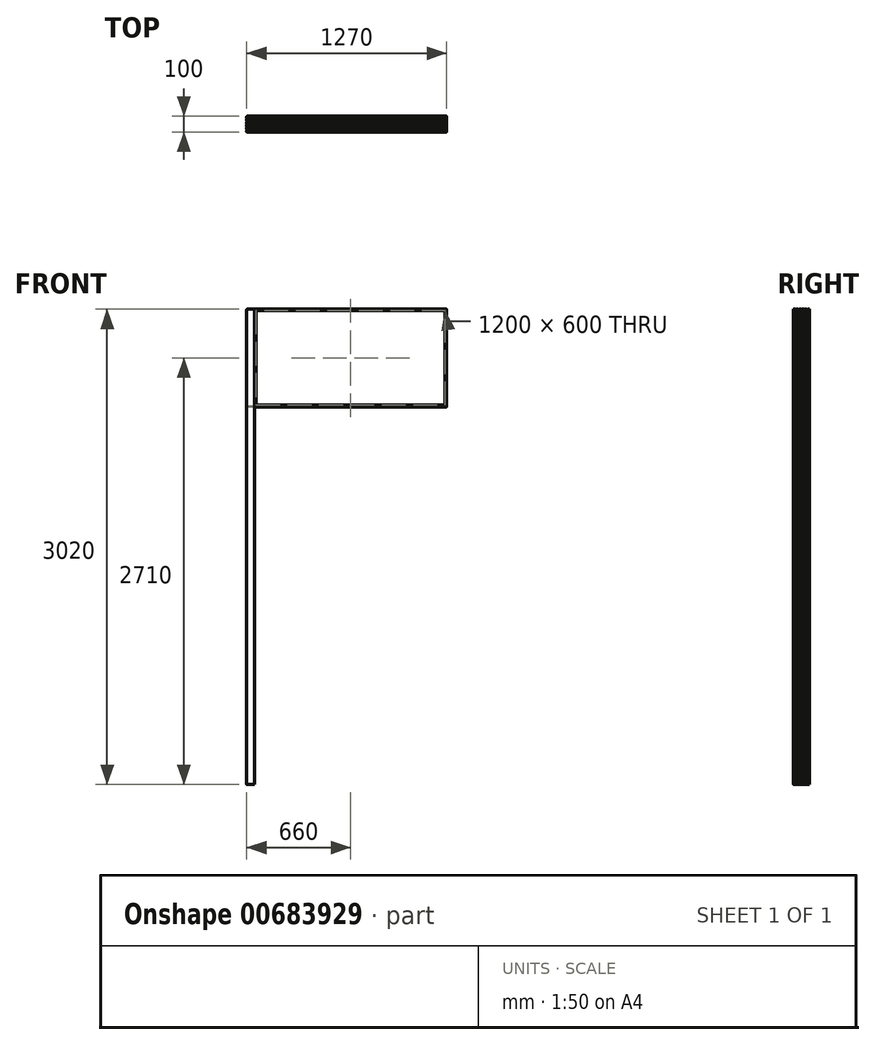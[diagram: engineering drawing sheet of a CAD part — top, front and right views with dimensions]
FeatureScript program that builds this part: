
annotation { "Feature Type Name" : "Feature", "Feature Type Description" : "" }
export const myFeature = defineFeature(function(context is Context, id is Id, definition is map)
    precondition{}
    {
        {
            var Q0;
            Q0=qCreatedBy(makeId("Front.planeOp"),FACE);
            var sketch = newSketch(context, id + "F0", { "sketchPlane" : qUnion([Q0])});
            skLineSegment(sketch, "E0.bottom", {"start": v(-2550, 0) * mm, "end": v(-2500, 0) * mm});
            skLineSegment(sketch, "E0.top", {"start": v(-2550, -3020) * mm, "end": v(-2500, -3020) * mm});
            skLineSegment(sketch, "E0.left", {"start": v(-2550, 0) * mm, "end": v(-2550, -3020) * mm});
            skLineSegment(sketch, "E0.right", {"start": v(-2500, 0) * mm, "end": v(-2500, -3020) * mm});
            skLineSegment(sketch, "E1.MirrorCS", {"start": v(2550, -3020) * mm, "end": v(2500, -3020) * mm});
            skLineSegment(sketch, "E2.MirrorCS", {"start": v(2500, 0) * mm, "end": v(2500, -3020) * mm});
            skLineSegment(sketch, "E3.MirrorCS", {"start": v(2550, 0) * mm, "end": v(2500, 0) * mm});
            skLineSegment(sketch, "E4.MirrorCS", {"start": v(2550, 0) * mm, "end": v(2550, -3020) * mm});
            skSolve(sketch);
        }
        {
            var Q0;
            Q0 = qSketchRegion(id + "F0", true);
            extrude(context, id + "F1", {"entities" : qUnion([Q0]), "depth" : 100 * mm, "offsetDistance" : 25 * mm});
        }
        {
            var Q0;
            Q0=makeQuery(id+"F1.opExtrude","SWEPT_FACE",FACE,{"disambiguationData":[OSD([sQuery(id+"F0.wireOp",EDGE,"E0.bottom")])]});
            var sketch = newSketch(context, id + "F2", { "sketchPlane" : qUnion([Q0])});
            skLineSegment(sketch, "E5.bottom", {"start": v(-2550, -100) * mm, "end": v(-3770, -100) * mm});
            skLineSegment(sketch, "E5.top", {"start": v(-2550, 0) * mm, "end": v(-3770, 0) * mm});
            skLineSegment(sketch, "E5.left", {"start": v(-2550, -100) * mm, "end": v(-2550, 0) * mm});
            skLineSegment(sketch, "E5.right", {"start": v(-3770, -100) * mm, "end": v(-3770, 0) * mm});
            skLineSegment(sketch, "E6.bottom", {"start": v(-2500, -100) * mm, "end": v(2500, -100) * mm});
            skLineSegment(sketch, "E6.top", {"start": v(-2500, 0) * mm, "end": v(2500, 0) * mm});
            skLineSegment(sketch, "E6.left", {"start": v(-2500, -100) * mm, "end": v(-2500, 0) * mm});
            skLineSegment(sketch, "E6.right", {"start": v(2500, -100) * mm, "end": v(2500, 0) * mm});
            skLineSegment(sketch, "E7.bottom", {"start": v(2550, -100) * mm, "end": v(3770, -100) * mm});
            skLineSegment(sketch, "E7.top", {"start": v(2550, 0) * mm, "end": v(3770, 0) * mm});
            skLineSegment(sketch, "E7.left", {"start": v(2550, -100) * mm, "end": v(2550, 0) * mm});
            skLineSegment(sketch, "E7.right", {"start": v(3770, -100) * mm, "end": v(3770, 0) * mm});
            skSolve(sketch);
        }
        {
            var Q0;
            Q0 = qSketchRegion(id + "F2", true);
            extrude(context, id + "F3", {"entities" : qUnion([Q0]), "oppositeDirection" : true, "depth" : 620 * mm, "offsetDistance" : 25 * mm});
        }
        {
            var Q0;
            Q0=makeQuery(id+"F3.opExtrude","SWEPT_FACE",FACE,{"disambiguationData":[OSD([sQuery(id+"F2.wireOp",EDGE,"E6.bottom")])]});
            var sketch = newSketch(context, id + "F4", { "sketchPlane" : qUnion([Q0])});
            skLineSegment(sketch, "E8.0", {"start": v(-2560, -10) * mm, "end": v(-3760, -10) * mm});
            skLineSegment(sketch, "E8.1", {"start": v(-2560, -610) * mm, "end": v(-2560, -10) * mm});
            skLineSegment(sketch, "E8.2", {"start": v(-3760, -610) * mm, "end": v(-2560, -610) * mm});
            skLineSegment(sketch, "E8.3", {"start": v(-3760, -10) * mm, "end": v(-3760, -610) * mm});
            skLineSegment(sketch, "E9.0", {"start": v(2490, -10) * mm, "end": v(-2490, -10) * mm});
            skLineSegment(sketch, "E9.1", {"start": v(2490, -610) * mm, "end": v(2490, -10) * mm});
            skLineSegment(sketch, "E9.2", {"start": v(-2490, -610) * mm, "end": v(2490, -610) * mm});
            skLineSegment(sketch, "E9.3", {"start": v(-2490, -10) * mm, "end": v(-2490, -610) * mm});
            skLineSegment(sketch, "E10.0", {"start": v(3760, -10) * mm, "end": v(2560, -10) * mm});
            skLineSegment(sketch, "E10.1", {"start": v(3760, -610) * mm, "end": v(3760, -10) * mm});
            skLineSegment(sketch, "E10.2", {"start": v(2560, -610) * mm, "end": v(3760, -610) * mm});
            skLineSegment(sketch, "E10.3", {"start": v(2560, -10) * mm, "end": v(2560, -610) * mm});
            skSolve(sketch);
        }
        {
            var Q0;
            Q0 = qSketchRegion(id + "F4", true);
            extrude(context, id + "F5", {"entities" : qUnion([Q0]), "operationType" : NewBodyOperationType.REMOVE, "endBound" : BoundingType.THROUGH_ALL, "oppositeDirection" : true, "depth" : 25 * mm, "offsetDistance" : 25 * mm});
        }
        {
            var Q0;
            Q0=makeQuery(id+"F3.opExtrude","SWEPT_FACE",FACE,{"disambiguationData":[OSD([sQuery(id+"F2.wireOp",EDGE,"E5.right")])]});
            var sketch = newSketch(context, id + "F6", { "sketchPlane" : qUnion([Q0])});
            skLineSegment(sketch, "E11", {"start": v(10, 0) * mm, "end": v(10, -2) * mm});
            skLineSegment(sketch, "E12", {"start": v(10, -2) * mm, "end": v(18, -2) * mm});
            skLineSegment(sketch, "E13", {"start": v(18, -2) * mm, "end": v(18, 0) * mm});
            skLineSegment(sketch, "E14.1.0.0", {"start": v(36, -2) * mm, "end": v(36, 0) * mm});
            skLineSegment(sketch, "E14.1.0.1", {"start": v(28, -2) * mm, "end": v(36, -2) * mm});
            skLineSegment(sketch, "E14.1.0.2", {"start": v(28, 0) * mm, "end": v(28, -2) * mm});
            skLineSegment(sketch, "E14.2.0.0", {"start": v(54, -2) * mm, "end": v(54, 0) * mm});
            skLineSegment(sketch, "E14.2.0.1", {"start": v(46, -2) * mm, "end": v(54, -2) * mm});
            skLineSegment(sketch, "E14.2.0.2", {"start": v(46, 0) * mm, "end": v(46, -2) * mm});
            skLineSegment(sketch, "E14.3.0.0", {"start": v(72, -2) * mm, "end": v(72, 0) * mm});
            skLineSegment(sketch, "E14.3.0.1", {"start": v(64, -2) * mm, "end": v(72, -2) * mm});
            skLineSegment(sketch, "E14.3.0.2", {"start": v(64, 0) * mm, "end": v(64, -2) * mm});
            skLineSegment(sketch, "E14.4.0.0", {"start": v(90, -2) * mm, "end": v(90, 0) * mm});
            skLineSegment(sketch, "E14.4.0.1", {"start": v(82, -2) * mm, "end": v(90, -2) * mm});
            skLineSegment(sketch, "E14.4.0.2", {"start": v(82, 0) * mm, "end": v(82, -2) * mm});
            skLineSegment(sketch, "E14.direction1", {"start": v(10, -2) * mm, "end": v(28, -2) * mm, "construction": true});
            skLineSegment(sketch, "E15", {"start": v(10, 0) * mm, "end": v(18, 0) * mm});
            skLineSegment(sketch, "E16", {"start": v(28, 0) * mm, "end": v(36, 0) * mm});
            skLineSegment(sketch, "E17", {"start": v(46, 0) * mm, "end": v(54, 0) * mm});
            skLineSegment(sketch, "E18", {"start": v(64, 0) * mm, "end": v(72, 0) * mm});
            skLineSegment(sketch, "E19", {"start": v(82, 0) * mm, "end": v(90, 0) * mm});
            skLineSegment(sketch, "E20", {"start": v(100, -310) * mm, "end": v(0, -310) * mm, "construction": true});
            skLineSegment(sketch, "E21.MirrorCS", {"start": v(90, -618) * mm, "end": v(90, -620) * mm});
            skLineSegment(sketch, "E22.MirrorCS", {"start": v(64, -620) * mm, "end": v(64, -618) * mm});
            skLineSegment(sketch, "E23.MirrorCS", {"start": v(10, -620) * mm, "end": v(10, -618) * mm});
            skLineSegment(sketch, "E24.MirrorCS", {"start": v(18, -618) * mm, "end": v(18, -620) * mm});
            skLineSegment(sketch, "E25.MirrorCS", {"start": v(36, -618) * mm, "end": v(36, -620) * mm});
            skLineSegment(sketch, "E26.MirrorCS", {"start": v(28, -620) * mm, "end": v(28, -618) * mm});
            skLineSegment(sketch, "E27.MirrorCS", {"start": v(54, -618) * mm, "end": v(54, -620) * mm});
            skLineSegment(sketch, "E28.MirrorCS", {"start": v(46, -620) * mm, "end": v(46, -618) * mm});
            skLineSegment(sketch, "E29.MirrorCS", {"start": v(72, -618) * mm, "end": v(72, -620) * mm});
            skLineSegment(sketch, "E30.MirrorCS", {"start": v(82, -620) * mm, "end": v(82, -618) * mm});
            skLineSegment(sketch, "E31.MirrorCS", {"start": v(10, -620) * mm, "end": v(18, -620) * mm});
            skLineSegment(sketch, "E32.MirrorCS", {"start": v(10, -618) * mm, "end": v(18, -618) * mm});
            skLineSegment(sketch, "E33.MirrorCS", {"start": v(64, -618) * mm, "end": v(72, -618) * mm});
            skLineSegment(sketch, "E34.MirrorCS", {"start": v(64, -620) * mm, "end": v(72, -620) * mm});
            skLineSegment(sketch, "E35.MirrorCS", {"start": v(82, -620) * mm, "end": v(90, -620) * mm});
            skLineSegment(sketch, "E36.MirrorCS", {"start": v(28, -620) * mm, "end": v(36, -620) * mm});
            skLineSegment(sketch, "E37.MirrorCS", {"start": v(82, -618) * mm, "end": v(90, -618) * mm});
            skLineSegment(sketch, "E38.MirrorCS", {"start": v(10, -618) * mm, "end": v(28, -618) * mm, "construction": true});
            skLineSegment(sketch, "E39.MirrorCS", {"start": v(46, -620) * mm, "end": v(54, -620) * mm});
            skLineSegment(sketch, "E40.MirrorCS", {"start": v(28, -618) * mm, "end": v(36, -618) * mm});
            skLineSegment(sketch, "E41.MirrorCS", {"start": v(46, -618) * mm, "end": v(54, -618) * mm});
            skSolve(sketch);
        }
        {
            var Q0;
            Q0 = qSketchRegion(id + "F6", true);
            extrude(context, id + "F7", {"entities" : qUnion([Q0]), "operationType" : NewBodyOperationType.REMOVE, "endBound" : BoundingType.THROUGH_ALL, "oppositeDirection" : true, "depth" : 25 * mm, "offsetDistance" : 25 * mm});
        }
        {
            var Q0;
            {var subQ0=sQuery(id+"F2.wireOp",EDGE,"E5.top");var subQ1=sQuery(id+"F2.wireOp",EDGE,"E5.left");var subQ2=sQuery(id+"F2.wireOp",EDGE,"E5.right");Q0=makeQuery(id+"F7.boolean.opBoolean","SPLIT",FACE,{"disambiguationData":[TD([makeQuery(id+"F3.opExtrude","SWEPT_FACE",FACE,{"disambiguationData":[OSD([subQ0])]})])],"derivedFrom":makeQuery(id+"F3.opExtrude","CAP_FACE",FACE,{"disambiguationData":[OSD([sQuery(id+"F2.wireOp",EDGE,"E5.bottom"),subQ0,subQ1,subQ2])],"isStart":true})});}
            var sketch = newSketch(context, id + "F8", { "sketchPlane" : qUnion([Q0])});
            skLineSegment(sketch, "E42.bottom", {"start": v(-3768, -90) * mm, "end": v(-3770, -90) * mm});
            skLineSegment(sketch, "E42.top", {"start": v(-3768, -82) * mm, "end": v(-3770, -82) * mm});
            skLineSegment(sketch, "E42.left", {"start": v(-3768, -90) * mm, "end": v(-3768, -82) * mm});
            skLineSegment(sketch, "E42.right", {"start": v(-3770, -90) * mm, "end": v(-3770, -82) * mm});
            skLineSegment(sketch, "E43.0.1.0", {"start": v(-3768, -64) * mm, "end": v(-3770, -64) * mm});
            skLineSegment(sketch, "E43.0.1.1", {"start": v(-3768, -72) * mm, "end": v(-3770, -72) * mm});
            skLineSegment(sketch, "E43.0.1.2", {"start": v(-3770, -72) * mm, "end": v(-3770, -64) * mm});
            skLineSegment(sketch, "E43.0.1.3", {"start": v(-3768, -72) * mm, "end": v(-3768, -64) * mm});
            skLineSegment(sketch, "E43.0.2.0", {"start": v(-3768, -46) * mm, "end": v(-3770, -46) * mm});
            skLineSegment(sketch, "E43.0.2.1", {"start": v(-3768, -54) * mm, "end": v(-3770, -54) * mm});
            skLineSegment(sketch, "E43.0.2.2", {"start": v(-3770, -54) * mm, "end": v(-3770, -46) * mm});
            skLineSegment(sketch, "E43.0.2.3", {"start": v(-3768, -54) * mm, "end": v(-3768, -46) * mm});
            skLineSegment(sketch, "E43.0.3.0", {"start": v(-3768, -28) * mm, "end": v(-3770, -28) * mm});
            skLineSegment(sketch, "E43.0.3.1", {"start": v(-3768, -36) * mm, "end": v(-3770, -36) * mm});
            skLineSegment(sketch, "E43.0.3.2", {"start": v(-3770, -36) * mm, "end": v(-3770, -28) * mm});
            skLineSegment(sketch, "E43.0.3.3", {"start": v(-3768, -36) * mm, "end": v(-3768, -28) * mm});
            skLineSegment(sketch, "E43.0.4.0", {"start": v(-3768, -10) * mm, "end": v(-3770, -10) * mm});
            skLineSegment(sketch, "E43.0.4.1", {"start": v(-3768, -18) * mm, "end": v(-3770, -18) * mm});
            skLineSegment(sketch, "E43.0.4.2", {"start": v(-3770, -18) * mm, "end": v(-3770, -10) * mm});
            skLineSegment(sketch, "E43.0.4.3", {"start": v(-3768, -18) * mm, "end": v(-3768, -10) * mm});
            skLineSegment(sketch, "E43.direction1", {"start": v(-3770, -90) * mm, "end": v(-2770, -90) * mm, "construction": true});
            skLineSegment(sketch, "E43.direction2", {"start": v(-3770, -90) * mm, "end": v(-3770, -72) * mm, "construction": true});
            skPoint(sketch, "E44.0", {"position": v(0, -10) * mm});
            skLineSegment(sketch, "E45.MirrorCS", {"start": v(3768, -64) * mm, "end": v(3770, -64) * mm});
            skLineSegment(sketch, "E46.MirrorCS", {"start": v(3768, -36) * mm, "end": v(3770, -36) * mm});
            skLineSegment(sketch, "E47.MirrorCS", {"start": v(3768, -90) * mm, "end": v(3770, -90) * mm});
            skLineSegment(sketch, "E48.MirrorCS", {"start": v(3768, -82) * mm, "end": v(3770, -82) * mm});
            skLineSegment(sketch, "E49.MirrorCS", {"start": v(3768, -72) * mm, "end": v(3770, -72) * mm});
            skLineSegment(sketch, "E50.MirrorCS", {"start": v(3768, -46) * mm, "end": v(3770, -46) * mm});
            skLineSegment(sketch, "E51.MirrorCS", {"start": v(3768, -54) * mm, "end": v(3770, -54) * mm});
            skLineSegment(sketch, "E52.MirrorCS", {"start": v(3770, -36) * mm, "end": v(3770, -28) * mm});
            skLineSegment(sketch, "E53.MirrorCS", {"start": v(3768, -90) * mm, "end": v(3768, -82) * mm});
            skLineSegment(sketch, "E54.MirrorCS", {"start": v(3770, -72) * mm, "end": v(3770, -64) * mm});
            skLineSegment(sketch, "E55.MirrorCS", {"start": v(3770, -54) * mm, "end": v(3770, -46) * mm});
            skLineSegment(sketch, "E56.MirrorCS", {"start": v(3768, -36) * mm, "end": v(3768, -28) * mm});
            skLineSegment(sketch, "E57.MirrorCS", {"start": v(3770, -90) * mm, "end": v(3770, -82) * mm});
            skLineSegment(sketch, "E58.MirrorCS", {"start": v(3768, -72) * mm, "end": v(3768, -64) * mm});
            skLineSegment(sketch, "E59.MirrorCS", {"start": v(3768, -54) * mm, "end": v(3768, -46) * mm});
            skLineSegment(sketch, "E60.MirrorCS", {"start": v(3768, -28) * mm, "end": v(3770, -28) * mm});
            skLineSegment(sketch, "E61.MirrorCS", {"start": v(3770, -90) * mm, "end": v(3770, -72) * mm, "construction": true});
            skLineSegment(sketch, "E62.MirrorCS", {"start": v(3770, -90) * mm, "end": v(2770, -90) * mm, "construction": true});
            skLineSegment(sketch, "E63.MirrorCS", {"start": v(3768, -18) * mm, "end": v(3770, -18) * mm});
            skLineSegment(sketch, "E64.MirrorCS", {"start": v(3770, -18) * mm, "end": v(3770, -10) * mm});
            skLineSegment(sketch, "E65.MirrorCS", {"start": v(3768, -18) * mm, "end": v(3768, -10) * mm});
            skLineSegment(sketch, "E66.MirrorCS", {"start": v(3768, -10) * mm, "end": v(3770, -10) * mm});
            skSolve(sketch);
        }
        {
            var Q0;
            Q0 = qSketchRegion(id + "F8", true);
            extrude(context, id + "F9", {"entities" : qUnion([Q0]), "operationType" : NewBodyOperationType.REMOVE, "endBound" : BoundingType.THROUGH_ALL, "oppositeDirection" : true, "depth" : 25 * mm, "offsetDistance" : 25 * mm});
        }
        {
            var Q0;
            Q0=makeQuery(id+"F3.opExtrude","SWEPT_FACE",FACE,{"disambiguationData":[OSD([sQuery(id+"F2.wireOp",EDGE,"E7.top")])]});
            cPlane(context, id + "F10", {"entities" : qUnion([Q0]), "cplaneType" : CPlaneType.OFFSET, "offset" : 1 * mm, "oppositeDirection" : true, "width" : 150 * mm, "height" : 150 * mm});
        }
        {
            var Q0;
            Q0=qCreatedBy(id+"F10.planeOp",FACE);
            var sketch = newSketch(context, id + "F11", { "sketchPlane" : qUnion([Q0])});
            skLineSegment(sketch, "E67.0", {"start": v(2490, -10) * mm, "end": v(2490, -610) * mm});
            skLineSegment(sketch, "E67.1", {"start": v(-2490, -10) * mm, "end": v(2490, -10) * mm});
            skLineSegment(sketch, "E67.2", {"start": v(2490, -610) * mm, "end": v(-2490, -610) * mm});
            skLineSegment(sketch, "E67.3", {"start": v(-2490, -610) * mm, "end": v(-2490, -10) * mm});
            skLineSegment(sketch, "E67.4", {"start": v(-2560, -10) * mm, "end": v(-2560, -610) * mm});
            skLineSegment(sketch, "E67.5", {"start": v(-2560, -610) * mm, "end": v(-3760, -610) * mm});
            skLineSegment(sketch, "E67.6", {"start": v(-3760, -10) * mm, "end": v(-2560, -10) * mm});
            skLineSegment(sketch, "E67.7", {"start": v(-3760, -610) * mm, "end": v(-3760, -10) * mm});
            skLineSegment(sketch, "E67.8", {"start": v(2560, -10) * mm, "end": v(2560, -610) * mm});
            skLineSegment(sketch, "E67.9", {"start": v(2560, -610) * mm, "end": v(3760, -610) * mm});
            skLineSegment(sketch, "E67.10", {"start": v(3760, -10) * mm, "end": v(2560, -10) * mm});
            skLineSegment(sketch, "E67.11", {"start": v(3760, -610) * mm, "end": v(3760, -10) * mm});
            skSolve(sketch);
        }
        {
            var Q0;
            Q0 = qSketchRegion(id + "F11", true);
            var Q1;
            Q1=makeQuery(id+"F3.opExtrude","SWEPT_FACE",FACE,{"disambiguationData":[OSD([sQuery(id+"F2.wireOp",EDGE,"E5.bottom")])]});
            extrude(context, id + "F12", {"entities" : qUnion([Q0]), "endBound" : BoundingType.UP_TO_SURFACE, "oppositeDirection" : true, "depth" : 25 * mm, "endBoundEntityFace" : qUnion([Q1]), "hasOffset" : true, "offsetDistance" : 1 * mm});
        }
        {
            var Q0;
            {var subQ0=sQuery(id+"F2.wireOp",EDGE,"E7.right");var subQ1=sQuery(id+"F2.wireOp",EDGE,"E7.top");Q0=makeQuery(id+"F7.boolean.opBoolean","SPLIT",EDGE,{"disambiguationData":[TD([makeQuery(id+"F3.opExtrude","SWEPT_FACE",FACE,{"disambiguationData":[OSD([subQ1])]})])],"derivedFrom":makeQuery(id+"F3.opExtrude","CAP_EDGE",EDGE,{"disambiguationData":[OSD([subQ0])],"isStart":true})});}
            var Q1;
            {var subQ0=sQuery(id+"F2.wireOp",EDGE,"E7.right");Q1=makeQuery(id+"F7.boolean.opBoolean","SPLIT",EDGE,{"disambiguationData":[TD([makeQuery(id+"F7.opExtrude","SWEPT_FACE",FACE,{"disambiguationData":[OSD([sQuery(id+"F6.wireOp",EDGE,"E13")])]})])],"derivedFrom":makeQuery(id+"F3.opExtrude","CAP_EDGE",EDGE,{"disambiguationData":[OSD([subQ0])],"isStart":true})});}
            var Q2;
            {var subQ0=sQuery(id+"F2.wireOp",EDGE,"E7.right");Q2=makeQuery(id+"F7.boolean.opBoolean","SPLIT",EDGE,{"disambiguationData":[TD([makeQuery(id+"F7.opExtrude","SWEPT_FACE",FACE,{"disambiguationData":[OSD([sQuery(id+"F6.wireOp",EDGE,"E14.1.0.0")])]})])],"derivedFrom":makeQuery(id+"F3.opExtrude","CAP_EDGE",EDGE,{"disambiguationData":[OSD([subQ0])],"isStart":true})});}
            var Q3;
            {var subQ0=sQuery(id+"F2.wireOp",EDGE,"E7.right");Q3=makeQuery(id+"F7.boolean.opBoolean","SPLIT",EDGE,{"disambiguationData":[TD([makeQuery(id+"F7.opExtrude","SWEPT_FACE",FACE,{"disambiguationData":[OSD([sQuery(id+"F6.wireOp",EDGE,"E14.2.0.0")])]})])],"derivedFrom":makeQuery(id+"F3.opExtrude","CAP_EDGE",EDGE,{"disambiguationData":[OSD([subQ0])],"isStart":true})});}
            var Q4;
            {var subQ0=sQuery(id+"F2.wireOp",EDGE,"E7.right");Q4=makeQuery(id+"F7.boolean.opBoolean","SPLIT",EDGE,{"disambiguationData":[TD([makeQuery(id+"F7.opExtrude","SWEPT_FACE",FACE,{"disambiguationData":[OSD([sQuery(id+"F6.wireOp",EDGE,"E14.3.0.0")])]})])],"derivedFrom":makeQuery(id+"F3.opExtrude","CAP_EDGE",EDGE,{"disambiguationData":[OSD([subQ0])],"isStart":true})});}
            var Q5;
            {var subQ0=sQuery(id+"F2.wireOp",EDGE,"E7.bottom");var subQ1=sQuery(id+"F2.wireOp",EDGE,"E7.right");Q5=makeQuery(id+"F7.boolean.opBoolean","SPLIT",EDGE,{"disambiguationData":[TD([makeQuery(id+"F3.opExtrude","SWEPT_FACE",FACE,{"disambiguationData":[OSD([subQ0])]})])],"derivedFrom":makeQuery(id+"F3.opExtrude","CAP_EDGE",EDGE,{"disambiguationData":[OSD([subQ1])],"isStart":true})});}
            var Q6;
            Q6=makeQuery(id+"F9.boolean.opBoolean","INTERSECT",EDGE,{"derivedFrom":[makeQuery(id+"F7.boolean.opBoolean","COPY",FACE,{"disambiguationData":[TD([makeQuery(id+"F3.opExtrude","SWEPT_FACE",FACE,{"disambiguationData":[OSD([sQuery(id+"F2.wireOp",EDGE,"E7.left")])]})])],"derivedFrom":makeQuery(id+"F7.opExtrude","SWEPT_FACE",FACE,{"disambiguationData":[OSD([sQuery(id+"F6.wireOp",EDGE,"E14.4.0.1")])]})}),makeQuery(id+"F9.opExtrude","SWEPT_FACE",FACE,{"disambiguationData":[OSD([sQuery(id+"F8.wireOp",EDGE,"E53.MirrorCS")])]})]});
            var Q7;
            Q7=makeQuery(id+"F9.boolean.opBoolean","INTERSECT",EDGE,{"derivedFrom":[makeQuery(id+"F7.boolean.opBoolean","COPY",FACE,{"disambiguationData":[TD([makeQuery(id+"F3.opExtrude","SWEPT_FACE",FACE,{"disambiguationData":[OSD([sQuery(id+"F2.wireOp",EDGE,"E7.left")])]})])],"derivedFrom":makeQuery(id+"F7.opExtrude","SWEPT_FACE",FACE,{"disambiguationData":[OSD([sQuery(id+"F6.wireOp",EDGE,"E14.3.0.1")])]})}),makeQuery(id+"F9.opExtrude","SWEPT_FACE",FACE,{"disambiguationData":[OSD([sQuery(id+"F8.wireOp",EDGE,"E58.MirrorCS")])]})]});
            var Q8;
            Q8=makeQuery(id+"F9.boolean.opBoolean","INTERSECT",EDGE,{"derivedFrom":[makeQuery(id+"F7.boolean.opBoolean","COPY",FACE,{"disambiguationData":[TD([makeQuery(id+"F3.opExtrude","SWEPT_FACE",FACE,{"disambiguationData":[OSD([sQuery(id+"F2.wireOp",EDGE,"E7.left")])]})])],"derivedFrom":makeQuery(id+"F7.opExtrude","SWEPT_FACE",FACE,{"disambiguationData":[OSD([sQuery(id+"F6.wireOp",EDGE,"E14.2.0.1")])]})}),makeQuery(id+"F9.opExtrude","SWEPT_FACE",FACE,{"disambiguationData":[OSD([sQuery(id+"F8.wireOp",EDGE,"E59.MirrorCS")])]})]});
            var Q9;
            Q9=makeQuery(id+"F9.boolean.opBoolean","INTERSECT",EDGE,{"derivedFrom":[makeQuery(id+"F7.boolean.opBoolean","COPY",FACE,{"disambiguationData":[TD([makeQuery(id+"F3.opExtrude","SWEPT_FACE",FACE,{"disambiguationData":[OSD([sQuery(id+"F2.wireOp",EDGE,"E7.left")])]})])],"derivedFrom":makeQuery(id+"F7.opExtrude","SWEPT_FACE",FACE,{"disambiguationData":[OSD([sQuery(id+"F6.wireOp",EDGE,"E14.1.0.1")])]})}),makeQuery(id+"F9.opExtrude","SWEPT_FACE",FACE,{"disambiguationData":[OSD([sQuery(id+"F8.wireOp",EDGE,"E56.MirrorCS")])]})]});
            var Q10;
            Q10=makeQuery(id+"F9.boolean.opBoolean","INTERSECT",EDGE,{"derivedFrom":[makeQuery(id+"F7.boolean.opBoolean","COPY",FACE,{"disambiguationData":[TD([makeQuery(id+"F3.opExtrude","SWEPT_FACE",FACE,{"disambiguationData":[OSD([sQuery(id+"F2.wireOp",EDGE,"E7.left")])]})])],"derivedFrom":makeQuery(id+"F7.opExtrude","SWEPT_FACE",FACE,{"disambiguationData":[OSD([sQuery(id+"F6.wireOp",EDGE,"E12")])]})}),makeQuery(id+"F9.opExtrude","SWEPT_FACE",FACE,{"disambiguationData":[OSD([sQuery(id+"F8.wireOp",EDGE,"E65.MirrorCS")])]})]});
            var Q11;
            {var subQ0=sQuery(id+"F2.wireOp",EDGE,"E7.left");var subQ1=sQuery(id+"F2.wireOp",EDGE,"E7.top");Q11=makeQuery(id+"F7.boolean.opBoolean","SPLIT",EDGE,{"disambiguationData":[TD([makeQuery(id+"F3.opExtrude","SWEPT_FACE",FACE,{"disambiguationData":[OSD([subQ1])]})])],"derivedFrom":makeQuery(id+"F3.opExtrude","CAP_EDGE",EDGE,{"disambiguationData":[OSD([subQ0])],"isStart":true})});}
            var Q12;
            {var subQ0=sQuery(id+"F2.wireOp",EDGE,"E7.left");Q12=makeQuery(id+"F7.boolean.opBoolean","SPLIT",EDGE,{"disambiguationData":[TD([makeQuery(id+"F7.opExtrude","SWEPT_FACE",FACE,{"disambiguationData":[OSD([sQuery(id+"F6.wireOp",EDGE,"E13")])]})])],"derivedFrom":makeQuery(id+"F3.opExtrude","CAP_EDGE",EDGE,{"disambiguationData":[OSD([subQ0])],"isStart":true})});}
            var Q13;
            {var subQ0=sQuery(id+"F2.wireOp",EDGE,"E7.left");Q13=makeQuery(id+"F7.boolean.opBoolean","SPLIT",EDGE,{"disambiguationData":[TD([makeQuery(id+"F7.opExtrude","SWEPT_FACE",FACE,{"disambiguationData":[OSD([sQuery(id+"F6.wireOp",EDGE,"E14.1.0.0")])]})])],"derivedFrom":makeQuery(id+"F3.opExtrude","CAP_EDGE",EDGE,{"disambiguationData":[OSD([subQ0])],"isStart":true})});}
            var Q14;
            {var subQ0=sQuery(id+"F2.wireOp",EDGE,"E7.left");Q14=makeQuery(id+"F7.boolean.opBoolean","SPLIT",EDGE,{"disambiguationData":[TD([makeQuery(id+"F7.opExtrude","SWEPT_FACE",FACE,{"disambiguationData":[OSD([sQuery(id+"F6.wireOp",EDGE,"E14.2.0.0")])]})])],"derivedFrom":makeQuery(id+"F3.opExtrude","CAP_EDGE",EDGE,{"disambiguationData":[OSD([subQ0])],"isStart":true})});}
            var Q15;
            {var subQ0=sQuery(id+"F2.wireOp",EDGE,"E7.bottom");var subQ1=sQuery(id+"F2.wireOp",EDGE,"E7.left");Q15=makeQuery(id+"F7.boolean.opBoolean","SPLIT",EDGE,{"disambiguationData":[TD([makeQuery(id+"F3.opExtrude","SWEPT_FACE",FACE,{"disambiguationData":[OSD([subQ0])]})])],"derivedFrom":makeQuery(id+"F3.opExtrude","CAP_EDGE",EDGE,{"disambiguationData":[OSD([subQ1])],"isStart":true})});}
            var Q16;
            Q16=makeQuery(id+"F1.opExtrude","SWEPT_EDGE",EDGE,{"disambiguationData":[OSD([sQuery(id+"F0.wireOp",EDGE,"E3.MirrorCS"),sQuery(id+"F0.wireOp",EDGE,"E4.MirrorCS")])]});
            var Q17;
            {var subQ0=sQuery(id+"F2.wireOp",EDGE,"E7.left");Q17=makeQuery(id+"F7.boolean.opBoolean","SPLIT",EDGE,{"disambiguationData":[TD([makeQuery(id+"F7.opExtrude","SWEPT_FACE",FACE,{"disambiguationData":[OSD([sQuery(id+"F6.wireOp",EDGE,"E14.3.0.0")])]})])],"derivedFrom":makeQuery(id+"F3.opExtrude","CAP_EDGE",EDGE,{"disambiguationData":[OSD([subQ0])],"isStart":true})});}
            var Q18;
            Q18=makeQuery(id+"F7.boolean.opBoolean","INTERSECT",EDGE,{"derivedFrom":[makeQuery(id+"F3.opExtrude","SWEPT_FACE",FACE,{"disambiguationData":[OSD([sQuery(id+"F2.wireOp",EDGE,"E7.left")])]}),makeQuery(id+"F7.opExtrude","SWEPT_FACE",FACE,{"disambiguationData":[OSD([sQuery(id+"F6.wireOp",EDGE,"E14.4.0.1")])]})]});
            var Q19;
            Q19=makeQuery(id+"F7.boolean.opBoolean","INTERSECT",EDGE,{"derivedFrom":[makeQuery(id+"F3.opExtrude","SWEPT_FACE",FACE,{"disambiguationData":[OSD([sQuery(id+"F2.wireOp",EDGE,"E7.left")])]}),makeQuery(id+"F7.opExtrude","SWEPT_FACE",FACE,{"disambiguationData":[OSD([sQuery(id+"F6.wireOp",EDGE,"E14.3.0.1")])]})]});
            var Q20;
            Q20=makeQuery(id+"F7.boolean.opBoolean","INTERSECT",EDGE,{"derivedFrom":[makeQuery(id+"F3.opExtrude","SWEPT_FACE",FACE,{"disambiguationData":[OSD([sQuery(id+"F2.wireOp",EDGE,"E7.left")])]}),makeQuery(id+"F7.opExtrude","SWEPT_FACE",FACE,{"disambiguationData":[OSD([sQuery(id+"F6.wireOp",EDGE,"E14.2.0.1")])]})]});
            var Q21;
            Q21=makeQuery(id+"F7.boolean.opBoolean","INTERSECT",EDGE,{"derivedFrom":[makeQuery(id+"F3.opExtrude","SWEPT_FACE",FACE,{"disambiguationData":[OSD([sQuery(id+"F2.wireOp",EDGE,"E7.left")])]}),makeQuery(id+"F7.opExtrude","SWEPT_FACE",FACE,{"disambiguationData":[OSD([sQuery(id+"F6.wireOp",EDGE,"E14.1.0.1")])]})]});
            var Q22;
            Q22=makeQuery(id+"F7.boolean.opBoolean","INTERSECT",EDGE,{"derivedFrom":[makeQuery(id+"F3.opExtrude","SWEPT_FACE",FACE,{"disambiguationData":[OSD([sQuery(id+"F2.wireOp",EDGE,"E7.left")])]}),makeQuery(id+"F7.opExtrude","SWEPT_FACE",FACE,{"disambiguationData":[OSD([sQuery(id+"F6.wireOp",EDGE,"E12")])]})]});
            var Q23;
            Q23=makeQuery(id+"F1.opExtrude","SWEPT_FACE",FACE,{"disambiguationData":[OSD([sQuery(id+"F0.wireOp",EDGE,"E3.MirrorCS")])]});
            var Q24;
            {var subQ0=sQuery(id+"F2.wireOp",EDGE,"E6.right");Q24=makeQuery(id+"F7.boolean.opBoolean","SPLIT",EDGE,{"disambiguationData":[TD([makeQuery(id+"F7.opExtrude","SWEPT_FACE",FACE,{"disambiguationData":[OSD([sQuery(id+"F6.wireOp",EDGE,"E14.1.0.0")])]})])],"derivedFrom":makeQuery(id+"F3.opExtrude","CAP_EDGE",EDGE,{"disambiguationData":[OSD([subQ0])],"isStart":true})});}
            var Q25;
            {var subQ0=sQuery(id+"F2.wireOp",EDGE,"E6.right");Q25=makeQuery(id+"F7.boolean.opBoolean","SPLIT",EDGE,{"disambiguationData":[TD([makeQuery(id+"F7.opExtrude","SWEPT_FACE",FACE,{"disambiguationData":[OSD([sQuery(id+"F6.wireOp",EDGE,"E13")])]})])],"derivedFrom":makeQuery(id+"F3.opExtrude","CAP_EDGE",EDGE,{"disambiguationData":[OSD([subQ0])],"isStart":true})});}
            var Q26;
            {var subQ0=sQuery(id+"F2.wireOp",EDGE,"E6.right");var subQ1=sQuery(id+"F2.wireOp",EDGE,"E6.top");Q26=makeQuery(id+"F7.boolean.opBoolean","SPLIT",EDGE,{"disambiguationData":[TD([makeQuery(id+"F3.opExtrude","SWEPT_FACE",FACE,{"disambiguationData":[OSD([subQ1])]})])],"derivedFrom":makeQuery(id+"F3.opExtrude","CAP_EDGE",EDGE,{"disambiguationData":[OSD([subQ0])],"isStart":true})});}
            var Q27;
            {var subQ0=sQuery(id+"F2.wireOp",EDGE,"E6.right");Q27=makeQuery(id+"F7.boolean.opBoolean","SPLIT",EDGE,{"disambiguationData":[TD([makeQuery(id+"F7.opExtrude","SWEPT_FACE",FACE,{"disambiguationData":[OSD([sQuery(id+"F6.wireOp",EDGE,"E14.2.0.0")])]})])],"derivedFrom":makeQuery(id+"F3.opExtrude","CAP_EDGE",EDGE,{"disambiguationData":[OSD([subQ0])],"isStart":true})});}
            var Q28;
            {var subQ0=sQuery(id+"F2.wireOp",EDGE,"E6.right");Q28=makeQuery(id+"F7.boolean.opBoolean","SPLIT",EDGE,{"disambiguationData":[TD([makeQuery(id+"F7.opExtrude","SWEPT_FACE",FACE,{"disambiguationData":[OSD([sQuery(id+"F6.wireOp",EDGE,"E14.3.0.0")])]})])],"derivedFrom":makeQuery(id+"F3.opExtrude","CAP_EDGE",EDGE,{"disambiguationData":[OSD([subQ0])],"isStart":true})});}
            var Q29;
            {var subQ0=sQuery(id+"F2.wireOp",EDGE,"E6.bottom");var subQ1=sQuery(id+"F2.wireOp",EDGE,"E6.right");Q29=makeQuery(id+"F7.boolean.opBoolean","SPLIT",EDGE,{"disambiguationData":[TD([makeQuery(id+"F3.opExtrude","SWEPT_FACE",FACE,{"disambiguationData":[OSD([subQ0])]})])],"derivedFrom":makeQuery(id+"F3.opExtrude","CAP_EDGE",EDGE,{"disambiguationData":[OSD([subQ1])],"isStart":true})});}
            var Q30;
            Q30=makeQuery(id+"F7.boolean.opBoolean","INTERSECT",EDGE,{"derivedFrom":[makeQuery(id+"F3.opExtrude","SWEPT_FACE",FACE,{"disambiguationData":[OSD([sQuery(id+"F2.wireOp",EDGE,"E6.right")])]}),makeQuery(id+"F7.opExtrude","SWEPT_FACE",FACE,{"disambiguationData":[OSD([sQuery(id+"F6.wireOp",EDGE,"E14.4.0.1")])]})]});
            var Q31;
            Q31=makeQuery(id+"F7.boolean.opBoolean","INTERSECT",EDGE,{"derivedFrom":[makeQuery(id+"F3.opExtrude","SWEPT_FACE",FACE,{"disambiguationData":[OSD([sQuery(id+"F2.wireOp",EDGE,"E6.right")])]}),makeQuery(id+"F7.opExtrude","SWEPT_FACE",FACE,{"disambiguationData":[OSD([sQuery(id+"F6.wireOp",EDGE,"E14.3.0.1")])]})]});
            var Q32;
            Q32=makeQuery(id+"F7.boolean.opBoolean","INTERSECT",EDGE,{"derivedFrom":[makeQuery(id+"F3.opExtrude","SWEPT_FACE",FACE,{"disambiguationData":[OSD([sQuery(id+"F2.wireOp",EDGE,"E6.right")])]}),makeQuery(id+"F7.opExtrude","SWEPT_FACE",FACE,{"disambiguationData":[OSD([sQuery(id+"F6.wireOp",EDGE,"E14.2.0.1")])]})]});
            var Q33;
            Q33=makeQuery(id+"F7.boolean.opBoolean","INTERSECT",EDGE,{"derivedFrom":[makeQuery(id+"F3.opExtrude","SWEPT_FACE",FACE,{"disambiguationData":[OSD([sQuery(id+"F2.wireOp",EDGE,"E6.right")])]}),makeQuery(id+"F7.opExtrude","SWEPT_FACE",FACE,{"disambiguationData":[OSD([sQuery(id+"F6.wireOp",EDGE,"E14.1.0.1")])]})]});
            var Q34;
            Q34=makeQuery(id+"F7.boolean.opBoolean","INTERSECT",EDGE,{"derivedFrom":[makeQuery(id+"F3.opExtrude","SWEPT_FACE",FACE,{"disambiguationData":[OSD([sQuery(id+"F2.wireOp",EDGE,"E6.right")])]}),makeQuery(id+"F7.opExtrude","SWEPT_FACE",FACE,{"disambiguationData":[OSD([sQuery(id+"F6.wireOp",EDGE,"E12")])]})]});
            var Q35;
            {var subQ0=sQuery(id+"F2.wireOp",EDGE,"E7.right");var subQ1=sQuery(id+"F2.wireOp",EDGE,"E7.top");Q35=makeQuery(id+"F7.boolean.opBoolean","SPLIT",EDGE,{"disambiguationData":[TD([makeQuery(id+"F3.opExtrude","SWEPT_FACE",FACE,{"disambiguationData":[OSD([subQ1])]})])],"derivedFrom":makeQuery(id+"F3.opExtrude","CAP_EDGE",EDGE,{"disambiguationData":[OSD([subQ0])],"isStart":false})});}
            var Q36;
            Q36=makeQuery(id+"F9.boolean.opBoolean","INTERSECT",EDGE,{"derivedFrom":[makeQuery(id+"F7.boolean.opBoolean","COPY",FACE,{"disambiguationData":[TD([makeQuery(id+"F3.opExtrude","SWEPT_FACE",FACE,{"disambiguationData":[OSD([sQuery(id+"F2.wireOp",EDGE,"E7.left")])]})])],"derivedFrom":makeQuery(id+"F7.opExtrude","SWEPT_FACE",FACE,{"disambiguationData":[OSD([sQuery(id+"F6.wireOp",EDGE,"E32.MirrorCS")])]})}),makeQuery(id+"F9.opExtrude","SWEPT_FACE",FACE,{"disambiguationData":[OSD([sQuery(id+"F8.wireOp",EDGE,"E65.MirrorCS")])]})]});
            var Q37;
            {var subQ0=sQuery(id+"F2.wireOp",EDGE,"E7.right");Q37=makeQuery(id+"F7.boolean.opBoolean","SPLIT",EDGE,{"disambiguationData":[TD([makeQuery(id+"F7.opExtrude","SWEPT_FACE",FACE,{"disambiguationData":[OSD([sQuery(id+"F6.wireOp",EDGE,"E24.MirrorCS")])]})])],"derivedFrom":makeQuery(id+"F3.opExtrude","CAP_EDGE",EDGE,{"disambiguationData":[OSD([subQ0])],"isStart":false})});}
            var Q38;
            Q38=makeQuery(id+"F9.boolean.opBoolean","INTERSECT",EDGE,{"derivedFrom":[makeQuery(id+"F7.boolean.opBoolean","COPY",FACE,{"disambiguationData":[TD([makeQuery(id+"F3.opExtrude","SWEPT_FACE",FACE,{"disambiguationData":[OSD([sQuery(id+"F2.wireOp",EDGE,"E7.left")])]})])],"derivedFrom":makeQuery(id+"F7.opExtrude","SWEPT_FACE",FACE,{"disambiguationData":[OSD([sQuery(id+"F6.wireOp",EDGE,"E40.MirrorCS")])]})}),makeQuery(id+"F9.opExtrude","SWEPT_FACE",FACE,{"disambiguationData":[OSD([sQuery(id+"F8.wireOp",EDGE,"E56.MirrorCS")])]})]});
            var Q39;
            {var subQ0=sQuery(id+"F2.wireOp",EDGE,"E7.right");Q39=makeQuery(id+"F7.boolean.opBoolean","SPLIT",EDGE,{"disambiguationData":[TD([makeQuery(id+"F7.opExtrude","SWEPT_FACE",FACE,{"disambiguationData":[OSD([sQuery(id+"F6.wireOp",EDGE,"E25.MirrorCS")])]})])],"derivedFrom":makeQuery(id+"F3.opExtrude","CAP_EDGE",EDGE,{"disambiguationData":[OSD([subQ0])],"isStart":false})});}
            var Q40;
            Q40=makeQuery(id+"F9.boolean.opBoolean","INTERSECT",EDGE,{"derivedFrom":[makeQuery(id+"F7.boolean.opBoolean","COPY",FACE,{"disambiguationData":[TD([makeQuery(id+"F3.opExtrude","SWEPT_FACE",FACE,{"disambiguationData":[OSD([sQuery(id+"F2.wireOp",EDGE,"E7.left")])]})])],"derivedFrom":makeQuery(id+"F7.opExtrude","SWEPT_FACE",FACE,{"disambiguationData":[OSD([sQuery(id+"F6.wireOp",EDGE,"E41.MirrorCS")])]})}),makeQuery(id+"F9.opExtrude","SWEPT_FACE",FACE,{"disambiguationData":[OSD([sQuery(id+"F8.wireOp",EDGE,"E59.MirrorCS")])]})]});
            var Q41;
            {var subQ0=sQuery(id+"F2.wireOp",EDGE,"E7.right");Q41=makeQuery(id+"F7.boolean.opBoolean","SPLIT",EDGE,{"disambiguationData":[TD([makeQuery(id+"F7.opExtrude","SWEPT_FACE",FACE,{"disambiguationData":[OSD([sQuery(id+"F6.wireOp",EDGE,"E22.MirrorCS")])]})])],"derivedFrom":makeQuery(id+"F3.opExtrude","CAP_EDGE",EDGE,{"disambiguationData":[OSD([subQ0])],"isStart":false})});}
            var Q42;
            Q42=makeQuery(id+"F9.boolean.opBoolean","INTERSECT",EDGE,{"derivedFrom":[makeQuery(id+"F7.boolean.opBoolean","COPY",FACE,{"disambiguationData":[TD([makeQuery(id+"F3.opExtrude","SWEPT_FACE",FACE,{"disambiguationData":[OSD([sQuery(id+"F2.wireOp",EDGE,"E7.left")])]})])],"derivedFrom":makeQuery(id+"F7.opExtrude","SWEPT_FACE",FACE,{"disambiguationData":[OSD([sQuery(id+"F6.wireOp",EDGE,"E33.MirrorCS")])]})}),makeQuery(id+"F9.opExtrude","SWEPT_FACE",FACE,{"disambiguationData":[OSD([sQuery(id+"F8.wireOp",EDGE,"E58.MirrorCS")])]})]});
            var Q43;
            {var subQ0=sQuery(id+"F2.wireOp",EDGE,"E7.right");Q43=makeQuery(id+"F7.boolean.opBoolean","SPLIT",EDGE,{"disambiguationData":[TD([makeQuery(id+"F7.opExtrude","SWEPT_FACE",FACE,{"disambiguationData":[OSD([sQuery(id+"F6.wireOp",EDGE,"E29.MirrorCS")])]})])],"derivedFrom":makeQuery(id+"F3.opExtrude","CAP_EDGE",EDGE,{"disambiguationData":[OSD([subQ0])],"isStart":false})});}
            var Q44;
            Q44=makeQuery(id+"F9.boolean.opBoolean","INTERSECT",EDGE,{"derivedFrom":[makeQuery(id+"F7.boolean.opBoolean","COPY",FACE,{"disambiguationData":[TD([makeQuery(id+"F3.opExtrude","SWEPT_FACE",FACE,{"disambiguationData":[OSD([sQuery(id+"F2.wireOp",EDGE,"E7.left")])]})])],"derivedFrom":makeQuery(id+"F7.opExtrude","SWEPT_FACE",FACE,{"disambiguationData":[OSD([sQuery(id+"F6.wireOp",EDGE,"E37.MirrorCS")])]})}),makeQuery(id+"F9.opExtrude","SWEPT_FACE",FACE,{"disambiguationData":[OSD([sQuery(id+"F8.wireOp",EDGE,"E53.MirrorCS")])]})]});
            var Q45;
            {var subQ0=sQuery(id+"F2.wireOp",EDGE,"E7.bottom");var subQ1=sQuery(id+"F2.wireOp",EDGE,"E7.right");Q45=makeQuery(id+"F7.boolean.opBoolean","SPLIT",EDGE,{"disambiguationData":[TD([makeQuery(id+"F3.opExtrude","SWEPT_FACE",FACE,{"disambiguationData":[OSD([subQ0])]})])],"derivedFrom":makeQuery(id+"F3.opExtrude","CAP_EDGE",EDGE,{"disambiguationData":[OSD([subQ1])],"isStart":false})});}
            var Q46;
            {var subQ0=sQuery(id+"F2.wireOp",EDGE,"E7.left");var subQ1=sQuery(id+"F2.wireOp",EDGE,"E7.top");Q46=makeQuery(id+"F7.boolean.opBoolean","SPLIT",EDGE,{"disambiguationData":[TD([makeQuery(id+"F3.opExtrude","SWEPT_FACE",FACE,{"disambiguationData":[OSD([subQ1])]})])],"derivedFrom":makeQuery(id+"F3.opExtrude","CAP_EDGE",EDGE,{"disambiguationData":[OSD([subQ0])],"isStart":false})});}
            var Q47;
            Q47=makeQuery(id+"F7.boolean.opBoolean","INTERSECT",EDGE,{"derivedFrom":[makeQuery(id+"F3.opExtrude","SWEPT_FACE",FACE,{"disambiguationData":[OSD([sQuery(id+"F2.wireOp",EDGE,"E7.left")])]}),makeQuery(id+"F7.opExtrude","SWEPT_FACE",FACE,{"disambiguationData":[OSD([sQuery(id+"F6.wireOp",EDGE,"E32.MirrorCS")])]})]});
            var Q48;
            {var subQ0=sQuery(id+"F2.wireOp",EDGE,"E7.left");Q48=makeQuery(id+"F7.boolean.opBoolean","SPLIT",EDGE,{"disambiguationData":[TD([makeQuery(id+"F7.opExtrude","SWEPT_FACE",FACE,{"disambiguationData":[OSD([sQuery(id+"F6.wireOp",EDGE,"E24.MirrorCS")])]})])],"derivedFrom":makeQuery(id+"F3.opExtrude","CAP_EDGE",EDGE,{"disambiguationData":[OSD([subQ0])],"isStart":false})});}
            var Q49;
            Q49=makeQuery(id+"F7.boolean.opBoolean","INTERSECT",EDGE,{"derivedFrom":[makeQuery(id+"F3.opExtrude","SWEPT_FACE",FACE,{"disambiguationData":[OSD([sQuery(id+"F2.wireOp",EDGE,"E7.left")])]}),makeQuery(id+"F7.opExtrude","SWEPT_FACE",FACE,{"disambiguationData":[OSD([sQuery(id+"F6.wireOp",EDGE,"E40.MirrorCS")])]})]});
            var Q50;
            {var subQ0=sQuery(id+"F2.wireOp",EDGE,"E7.left");Q50=makeQuery(id+"F7.boolean.opBoolean","SPLIT",EDGE,{"disambiguationData":[TD([makeQuery(id+"F7.opExtrude","SWEPT_FACE",FACE,{"disambiguationData":[OSD([sQuery(id+"F6.wireOp",EDGE,"E25.MirrorCS")])]})])],"derivedFrom":makeQuery(id+"F3.opExtrude","CAP_EDGE",EDGE,{"disambiguationData":[OSD([subQ0])],"isStart":false})});}
            var Q51;
            Q51=makeQuery(id+"F7.boolean.opBoolean","INTERSECT",EDGE,{"derivedFrom":[makeQuery(id+"F3.opExtrude","SWEPT_FACE",FACE,{"disambiguationData":[OSD([sQuery(id+"F2.wireOp",EDGE,"E7.left")])]}),makeQuery(id+"F7.opExtrude","SWEPT_FACE",FACE,{"disambiguationData":[OSD([sQuery(id+"F6.wireOp",EDGE,"E41.MirrorCS")])]})]});
            var Q52;
            {var subQ0=sQuery(id+"F2.wireOp",EDGE,"E7.left");Q52=makeQuery(id+"F7.boolean.opBoolean","SPLIT",EDGE,{"disambiguationData":[TD([makeQuery(id+"F7.opExtrude","SWEPT_FACE",FACE,{"disambiguationData":[OSD([sQuery(id+"F6.wireOp",EDGE,"E22.MirrorCS")])]})])],"derivedFrom":makeQuery(id+"F3.opExtrude","CAP_EDGE",EDGE,{"disambiguationData":[OSD([subQ0])],"isStart":false})});}
            var Q53;
            Q53=makeQuery(id+"F7.boolean.opBoolean","INTERSECT",EDGE,{"derivedFrom":[makeQuery(id+"F3.opExtrude","SWEPT_FACE",FACE,{"disambiguationData":[OSD([sQuery(id+"F2.wireOp",EDGE,"E7.left")])]}),makeQuery(id+"F7.opExtrude","SWEPT_FACE",FACE,{"disambiguationData":[OSD([sQuery(id+"F6.wireOp",EDGE,"E33.MirrorCS")])]})]});
            var Q54;
            {var subQ0=sQuery(id+"F2.wireOp",EDGE,"E7.left");Q54=makeQuery(id+"F7.boolean.opBoolean","SPLIT",EDGE,{"disambiguationData":[TD([makeQuery(id+"F7.opExtrude","SWEPT_FACE",FACE,{"disambiguationData":[OSD([sQuery(id+"F6.wireOp",EDGE,"E29.MirrorCS")])]})])],"derivedFrom":makeQuery(id+"F3.opExtrude","CAP_EDGE",EDGE,{"disambiguationData":[OSD([subQ0])],"isStart":false})});}
            var Q55;
            Q55=makeQuery(id+"F7.boolean.opBoolean","INTERSECT",EDGE,{"derivedFrom":[makeQuery(id+"F3.opExtrude","SWEPT_FACE",FACE,{"disambiguationData":[OSD([sQuery(id+"F2.wireOp",EDGE,"E7.left")])]}),makeQuery(id+"F7.opExtrude","SWEPT_FACE",FACE,{"disambiguationData":[OSD([sQuery(id+"F6.wireOp",EDGE,"E37.MirrorCS")])]})]});
            var Q56;
            {var subQ0=sQuery(id+"F2.wireOp",EDGE,"E7.bottom");var subQ1=sQuery(id+"F2.wireOp",EDGE,"E7.left");Q56=makeQuery(id+"F7.boolean.opBoolean","SPLIT",EDGE,{"disambiguationData":[TD([makeQuery(id+"F3.opExtrude","SWEPT_FACE",FACE,{"disambiguationData":[OSD([subQ0])]})])],"derivedFrom":makeQuery(id+"F3.opExtrude","CAP_EDGE",EDGE,{"disambiguationData":[OSD([subQ1])],"isStart":false})});}
            var Q57;
            {var subQ0=sQuery(id+"F2.wireOp",EDGE,"E6.bottom");var subQ1=sQuery(id+"F2.wireOp",EDGE,"E6.right");Q57=makeQuery(id+"F7.boolean.opBoolean","SPLIT",EDGE,{"disambiguationData":[TD([makeQuery(id+"F3.opExtrude","SWEPT_FACE",FACE,{"disambiguationData":[OSD([subQ0])]})])],"derivedFrom":makeQuery(id+"F3.opExtrude","CAP_EDGE",EDGE,{"disambiguationData":[OSD([subQ1])],"isStart":false})});}
            var Q58;
            Q58=makeQuery(id+"F7.boolean.opBoolean","INTERSECT",EDGE,{"derivedFrom":[makeQuery(id+"F3.opExtrude","SWEPT_FACE",FACE,{"disambiguationData":[OSD([sQuery(id+"F2.wireOp",EDGE,"E6.right")])]}),makeQuery(id+"F7.opExtrude","SWEPT_FACE",FACE,{"disambiguationData":[OSD([sQuery(id+"F6.wireOp",EDGE,"E37.MirrorCS")])]})]});
            var Q59;
            {var subQ0=sQuery(id+"F2.wireOp",EDGE,"E6.right");Q59=makeQuery(id+"F7.boolean.opBoolean","SPLIT",EDGE,{"disambiguationData":[TD([makeQuery(id+"F7.opExtrude","SWEPT_FACE",FACE,{"disambiguationData":[OSD([sQuery(id+"F6.wireOp",EDGE,"E29.MirrorCS")])]})])],"derivedFrom":makeQuery(id+"F3.opExtrude","CAP_EDGE",EDGE,{"disambiguationData":[OSD([subQ0])],"isStart":false})});}
            var Q60;
            Q60=makeQuery(id+"F7.boolean.opBoolean","INTERSECT",EDGE,{"derivedFrom":[makeQuery(id+"F3.opExtrude","SWEPT_FACE",FACE,{"disambiguationData":[OSD([sQuery(id+"F2.wireOp",EDGE,"E6.right")])]}),makeQuery(id+"F7.opExtrude","SWEPT_FACE",FACE,{"disambiguationData":[OSD([sQuery(id+"F6.wireOp",EDGE,"E33.MirrorCS")])]})]});
            var Q61;
            {var subQ0=sQuery(id+"F2.wireOp",EDGE,"E6.right");Q61=makeQuery(id+"F7.boolean.opBoolean","SPLIT",EDGE,{"disambiguationData":[TD([makeQuery(id+"F7.opExtrude","SWEPT_FACE",FACE,{"disambiguationData":[OSD([sQuery(id+"F6.wireOp",EDGE,"E22.MirrorCS")])]})])],"derivedFrom":makeQuery(id+"F3.opExtrude","CAP_EDGE",EDGE,{"disambiguationData":[OSD([subQ0])],"isStart":false})});}
            var Q62;
            Q62=makeQuery(id+"F7.boolean.opBoolean","INTERSECT",EDGE,{"derivedFrom":[makeQuery(id+"F3.opExtrude","SWEPT_FACE",FACE,{"disambiguationData":[OSD([sQuery(id+"F2.wireOp",EDGE,"E6.right")])]}),makeQuery(id+"F7.opExtrude","SWEPT_FACE",FACE,{"disambiguationData":[OSD([sQuery(id+"F6.wireOp",EDGE,"E41.MirrorCS")])]})]});
            var Q63;
            {var subQ0=sQuery(id+"F2.wireOp",EDGE,"E6.right");Q63=makeQuery(id+"F7.boolean.opBoolean","SPLIT",EDGE,{"disambiguationData":[TD([makeQuery(id+"F7.opExtrude","SWEPT_FACE",FACE,{"disambiguationData":[OSD([sQuery(id+"F6.wireOp",EDGE,"E25.MirrorCS")])]})])],"derivedFrom":makeQuery(id+"F3.opExtrude","CAP_EDGE",EDGE,{"disambiguationData":[OSD([subQ0])],"isStart":false})});}
            var Q64;
            Q64=makeQuery(id+"F7.boolean.opBoolean","INTERSECT",EDGE,{"derivedFrom":[makeQuery(id+"F3.opExtrude","SWEPT_FACE",FACE,{"disambiguationData":[OSD([sQuery(id+"F2.wireOp",EDGE,"E6.right")])]}),makeQuery(id+"F7.opExtrude","SWEPT_FACE",FACE,{"disambiguationData":[OSD([sQuery(id+"F6.wireOp",EDGE,"E40.MirrorCS")])]})]});
            var Q65;
            {var subQ0=sQuery(id+"F2.wireOp",EDGE,"E6.right");Q65=makeQuery(id+"F7.boolean.opBoolean","SPLIT",EDGE,{"disambiguationData":[TD([makeQuery(id+"F7.opExtrude","SWEPT_FACE",FACE,{"disambiguationData":[OSD([sQuery(id+"F6.wireOp",EDGE,"E24.MirrorCS")])]})])],"derivedFrom":makeQuery(id+"F3.opExtrude","CAP_EDGE",EDGE,{"disambiguationData":[OSD([subQ0])],"isStart":false})});}
            var Q66;
            Q66=makeQuery(id+"F7.boolean.opBoolean","INTERSECT",EDGE,{"derivedFrom":[makeQuery(id+"F3.opExtrude","SWEPT_FACE",FACE,{"disambiguationData":[OSD([sQuery(id+"F2.wireOp",EDGE,"E6.right")])]}),makeQuery(id+"F7.opExtrude","SWEPT_FACE",FACE,{"disambiguationData":[OSD([sQuery(id+"F6.wireOp",EDGE,"E32.MirrorCS")])]})]});
            var Q67;
            {var subQ0=sQuery(id+"F2.wireOp",EDGE,"E6.right");var subQ1=sQuery(id+"F2.wireOp",EDGE,"E6.top");Q67=makeQuery(id+"F7.boolean.opBoolean","SPLIT",EDGE,{"disambiguationData":[TD([makeQuery(id+"F3.opExtrude","SWEPT_FACE",FACE,{"disambiguationData":[OSD([subQ1])]})])],"derivedFrom":makeQuery(id+"F3.opExtrude","CAP_EDGE",EDGE,{"disambiguationData":[OSD([subQ0])],"isStart":false})});}
            var Q68;
            {var subQ0=sQuery(id+"F2.wireOp",EDGE,"E6.left");var subQ1=sQuery(id+"F2.wireOp",EDGE,"E6.top");Q68=makeQuery(id+"F7.boolean.opBoolean","SPLIT",EDGE,{"disambiguationData":[TD([makeQuery(id+"F3.opExtrude","SWEPT_FACE",FACE,{"disambiguationData":[OSD([subQ1])]})])],"derivedFrom":makeQuery(id+"F3.opExtrude","CAP_EDGE",EDGE,{"disambiguationData":[OSD([subQ0])],"isStart":false})});}
            var Q69;
            {var subQ0=sQuery(id+"F2.wireOp",EDGE,"E6.left");Q69=makeQuery(id+"F7.boolean.opBoolean","SPLIT",EDGE,{"disambiguationData":[TD([makeQuery(id+"F7.opExtrude","SWEPT_FACE",FACE,{"disambiguationData":[OSD([sQuery(id+"F6.wireOp",EDGE,"E24.MirrorCS")])]})])],"derivedFrom":makeQuery(id+"F3.opExtrude","CAP_EDGE",EDGE,{"disambiguationData":[OSD([subQ0])],"isStart":false})});}
            var Q70;
            Q70=makeQuery(id+"F7.boolean.opBoolean","INTERSECT",EDGE,{"derivedFrom":[makeQuery(id+"F3.opExtrude","SWEPT_FACE",FACE,{"disambiguationData":[OSD([sQuery(id+"F2.wireOp",EDGE,"E6.left")])]}),makeQuery(id+"F7.opExtrude","SWEPT_FACE",FACE,{"disambiguationData":[OSD([sQuery(id+"F6.wireOp",EDGE,"E40.MirrorCS")])]})]});
            var Q71;
            {var subQ0=sQuery(id+"F2.wireOp",EDGE,"E6.left");Q71=makeQuery(id+"F7.boolean.opBoolean","SPLIT",EDGE,{"disambiguationData":[TD([makeQuery(id+"F7.opExtrude","SWEPT_FACE",FACE,{"disambiguationData":[OSD([sQuery(id+"F6.wireOp",EDGE,"E25.MirrorCS")])]})])],"derivedFrom":makeQuery(id+"F3.opExtrude","CAP_EDGE",EDGE,{"disambiguationData":[OSD([subQ0])],"isStart":false})});}
            var Q72;
            Q72=makeQuery(id+"F7.boolean.opBoolean","INTERSECT",EDGE,{"derivedFrom":[makeQuery(id+"F3.opExtrude","SWEPT_FACE",FACE,{"disambiguationData":[OSD([sQuery(id+"F2.wireOp",EDGE,"E6.left")])]}),makeQuery(id+"F7.opExtrude","SWEPT_FACE",FACE,{"disambiguationData":[OSD([sQuery(id+"F6.wireOp",EDGE,"E41.MirrorCS")])]})]});
            var Q73;
            {var subQ0=sQuery(id+"F2.wireOp",EDGE,"E6.left");Q73=makeQuery(id+"F7.boolean.opBoolean","SPLIT",EDGE,{"disambiguationData":[TD([makeQuery(id+"F7.opExtrude","SWEPT_FACE",FACE,{"disambiguationData":[OSD([sQuery(id+"F6.wireOp",EDGE,"E22.MirrorCS")])]})])],"derivedFrom":makeQuery(id+"F3.opExtrude","CAP_EDGE",EDGE,{"disambiguationData":[OSD([subQ0])],"isStart":false})});}
            var Q74;
            Q74=makeQuery(id+"F7.boolean.opBoolean","INTERSECT",EDGE,{"derivedFrom":[makeQuery(id+"F3.opExtrude","SWEPT_FACE",FACE,{"disambiguationData":[OSD([sQuery(id+"F2.wireOp",EDGE,"E6.left")])]}),makeQuery(id+"F7.opExtrude","SWEPT_FACE",FACE,{"disambiguationData":[OSD([sQuery(id+"F6.wireOp",EDGE,"E33.MirrorCS")])]})]});
            var Q75;
            {var subQ0=sQuery(id+"F2.wireOp",EDGE,"E6.left");Q75=makeQuery(id+"F7.boolean.opBoolean","SPLIT",EDGE,{"disambiguationData":[TD([makeQuery(id+"F7.opExtrude","SWEPT_FACE",FACE,{"disambiguationData":[OSD([sQuery(id+"F6.wireOp",EDGE,"E29.MirrorCS")])]})])],"derivedFrom":makeQuery(id+"F3.opExtrude","CAP_EDGE",EDGE,{"disambiguationData":[OSD([subQ0])],"isStart":false})});}
            var Q76;
            Q76=makeQuery(id+"F7.boolean.opBoolean","INTERSECT",EDGE,{"derivedFrom":[makeQuery(id+"F3.opExtrude","SWEPT_FACE",FACE,{"disambiguationData":[OSD([sQuery(id+"F2.wireOp",EDGE,"E6.left")])]}),makeQuery(id+"F7.opExtrude","SWEPT_FACE",FACE,{"disambiguationData":[OSD([sQuery(id+"F6.wireOp",EDGE,"E37.MirrorCS")])]})]});
            var Q77;
            {var subQ0=sQuery(id+"F2.wireOp",EDGE,"E6.bottom");var subQ1=sQuery(id+"F2.wireOp",EDGE,"E6.left");Q77=makeQuery(id+"F7.boolean.opBoolean","SPLIT",EDGE,{"disambiguationData":[TD([makeQuery(id+"F3.opExtrude","SWEPT_FACE",FACE,{"disambiguationData":[OSD([subQ0])]})])],"derivedFrom":makeQuery(id+"F3.opExtrude","CAP_EDGE",EDGE,{"disambiguationData":[OSD([subQ1])],"isStart":false})});}
            var Q78;
            Q78=makeQuery(id+"F7.boolean.opBoolean","INTERSECT",EDGE,{"derivedFrom":[makeQuery(id+"F3.opExtrude","SWEPT_FACE",FACE,{"disambiguationData":[OSD([sQuery(id+"F2.wireOp",EDGE,"E6.left")])]}),makeQuery(id+"F7.opExtrude","SWEPT_FACE",FACE,{"disambiguationData":[OSD([sQuery(id+"F6.wireOp",EDGE,"E32.MirrorCS")])]})]});
            var Q79;
            {var subQ0=sQuery(id+"F2.wireOp",EDGE,"E5.left");var subQ1=sQuery(id+"F2.wireOp",EDGE,"E5.top");Q79=makeQuery(id+"F7.boolean.opBoolean","SPLIT",EDGE,{"disambiguationData":[TD([makeQuery(id+"F3.opExtrude","SWEPT_FACE",FACE,{"disambiguationData":[OSD([subQ1])]})])],"derivedFrom":makeQuery(id+"F3.opExtrude","CAP_EDGE",EDGE,{"disambiguationData":[OSD([subQ0])],"isStart":false})});}
            var Q80;
            Q80=makeQuery(id+"F7.boolean.opBoolean","INTERSECT",EDGE,{"derivedFrom":[makeQuery(id+"F3.opExtrude","SWEPT_FACE",FACE,{"disambiguationData":[OSD([sQuery(id+"F2.wireOp",EDGE,"E5.left")])]}),makeQuery(id+"F7.opExtrude","SWEPT_FACE",FACE,{"disambiguationData":[OSD([sQuery(id+"F6.wireOp",EDGE,"E32.MirrorCS")])]})]});
            var Q81;
            {var subQ0=sQuery(id+"F2.wireOp",EDGE,"E5.left");Q81=makeQuery(id+"F7.boolean.opBoolean","SPLIT",EDGE,{"disambiguationData":[TD([makeQuery(id+"F7.opExtrude","SWEPT_FACE",FACE,{"disambiguationData":[OSD([sQuery(id+"F6.wireOp",EDGE,"E24.MirrorCS")])]})])],"derivedFrom":makeQuery(id+"F3.opExtrude","CAP_EDGE",EDGE,{"disambiguationData":[OSD([subQ0])],"isStart":false})});}
            var Q82;
            Q82=makeQuery(id+"F7.boolean.opBoolean","INTERSECT",EDGE,{"derivedFrom":[makeQuery(id+"F3.opExtrude","SWEPT_FACE",FACE,{"disambiguationData":[OSD([sQuery(id+"F2.wireOp",EDGE,"E5.left")])]}),makeQuery(id+"F7.opExtrude","SWEPT_FACE",FACE,{"disambiguationData":[OSD([sQuery(id+"F6.wireOp",EDGE,"E40.MirrorCS")])]})]});
            var Q83;
            {var subQ0=sQuery(id+"F2.wireOp",EDGE,"E5.left");Q83=makeQuery(id+"F7.boolean.opBoolean","SPLIT",EDGE,{"disambiguationData":[TD([makeQuery(id+"F7.opExtrude","SWEPT_FACE",FACE,{"disambiguationData":[OSD([sQuery(id+"F6.wireOp",EDGE,"E25.MirrorCS")])]})])],"derivedFrom":makeQuery(id+"F3.opExtrude","CAP_EDGE",EDGE,{"disambiguationData":[OSD([subQ0])],"isStart":false})});}
            var Q84;
            Q84=makeQuery(id+"F7.boolean.opBoolean","INTERSECT",EDGE,{"derivedFrom":[makeQuery(id+"F3.opExtrude","SWEPT_FACE",FACE,{"disambiguationData":[OSD([sQuery(id+"F2.wireOp",EDGE,"E5.left")])]}),makeQuery(id+"F7.opExtrude","SWEPT_FACE",FACE,{"disambiguationData":[OSD([sQuery(id+"F6.wireOp",EDGE,"E41.MirrorCS")])]})]});
            var Q85;
            {var subQ0=sQuery(id+"F2.wireOp",EDGE,"E5.left");Q85=makeQuery(id+"F7.boolean.opBoolean","SPLIT",EDGE,{"disambiguationData":[TD([makeQuery(id+"F7.opExtrude","SWEPT_FACE",FACE,{"disambiguationData":[OSD([sQuery(id+"F6.wireOp",EDGE,"E22.MirrorCS")])]})])],"derivedFrom":makeQuery(id+"F3.opExtrude","CAP_EDGE",EDGE,{"disambiguationData":[OSD([subQ0])],"isStart":false})});}
            var Q86;
            Q86=makeQuery(id+"F7.boolean.opBoolean","INTERSECT",EDGE,{"derivedFrom":[makeQuery(id+"F3.opExtrude","SWEPT_FACE",FACE,{"disambiguationData":[OSD([sQuery(id+"F2.wireOp",EDGE,"E5.left")])]}),makeQuery(id+"F7.opExtrude","SWEPT_FACE",FACE,{"disambiguationData":[OSD([sQuery(id+"F6.wireOp",EDGE,"E33.MirrorCS")])]})]});
            var Q87;
            {var subQ0=sQuery(id+"F2.wireOp",EDGE,"E5.left");Q87=makeQuery(id+"F7.boolean.opBoolean","SPLIT",EDGE,{"disambiguationData":[TD([makeQuery(id+"F7.opExtrude","SWEPT_FACE",FACE,{"disambiguationData":[OSD([sQuery(id+"F6.wireOp",EDGE,"E29.MirrorCS")])]})])],"derivedFrom":makeQuery(id+"F3.opExtrude","CAP_EDGE",EDGE,{"disambiguationData":[OSD([subQ0])],"isStart":false})});}
            var Q88;
            Q88=makeQuery(id+"F7.boolean.opBoolean","INTERSECT",EDGE,{"derivedFrom":[makeQuery(id+"F3.opExtrude","SWEPT_FACE",FACE,{"disambiguationData":[OSD([sQuery(id+"F2.wireOp",EDGE,"E5.left")])]}),makeQuery(id+"F7.opExtrude","SWEPT_FACE",FACE,{"disambiguationData":[OSD([sQuery(id+"F6.wireOp",EDGE,"E37.MirrorCS")])]})]});
            var Q89;
            {var subQ0=sQuery(id+"F2.wireOp",EDGE,"E5.bottom");var subQ1=sQuery(id+"F2.wireOp",EDGE,"E5.left");Q89=makeQuery(id+"F7.boolean.opBoolean","SPLIT",EDGE,{"disambiguationData":[TD([makeQuery(id+"F3.opExtrude","SWEPT_FACE",FACE,{"disambiguationData":[OSD([subQ0])]})])],"derivedFrom":makeQuery(id+"F3.opExtrude","CAP_EDGE",EDGE,{"disambiguationData":[OSD([subQ1])],"isStart":false})});}
            var Q90;
            {var subQ0=sQuery(id+"F2.wireOp",EDGE,"E5.bottom");var subQ1=sQuery(id+"F2.wireOp",EDGE,"E5.right");Q90=makeQuery(id+"F7.boolean.opBoolean","SPLIT",EDGE,{"disambiguationData":[TD([makeQuery(id+"F3.opExtrude","SWEPT_FACE",FACE,{"disambiguationData":[OSD([subQ0])]})])],"derivedFrom":makeQuery(id+"F3.opExtrude","CAP_EDGE",EDGE,{"disambiguationData":[OSD([subQ1])],"isStart":false})});}
            var Q91;
            Q91=makeQuery(id+"F9.boolean.opBoolean","INTERSECT",EDGE,{"derivedFrom":[makeQuery(id+"F7.boolean.opBoolean","COPY",FACE,{"disambiguationData":[TD([makeQuery(id+"F3.opExtrude","SWEPT_FACE",FACE,{"disambiguationData":[OSD([sQuery(id+"F2.wireOp",EDGE,"E5.left")])]})])],"derivedFrom":makeQuery(id+"F7.opExtrude","SWEPT_FACE",FACE,{"disambiguationData":[OSD([sQuery(id+"F6.wireOp",EDGE,"E37.MirrorCS")])]})}),makeQuery(id+"F9.opExtrude","SWEPT_FACE",FACE,{"disambiguationData":[OSD([sQuery(id+"F8.wireOp",EDGE,"E42.left")])]})]});
            var Q92;
            {var subQ0=sQuery(id+"F2.wireOp",EDGE,"E5.right");Q92=makeQuery(id+"F7.boolean.opBoolean","SPLIT",EDGE,{"disambiguationData":[TD([makeQuery(id+"F7.opExtrude","SWEPT_FACE",FACE,{"disambiguationData":[OSD([sQuery(id+"F6.wireOp",EDGE,"E29.MirrorCS")])]})])],"derivedFrom":makeQuery(id+"F3.opExtrude","CAP_EDGE",EDGE,{"disambiguationData":[OSD([subQ0])],"isStart":false})});}
            var Q93;
            Q93=makeQuery(id+"F9.boolean.opBoolean","INTERSECT",EDGE,{"derivedFrom":[makeQuery(id+"F7.boolean.opBoolean","COPY",FACE,{"disambiguationData":[TD([makeQuery(id+"F3.opExtrude","SWEPT_FACE",FACE,{"disambiguationData":[OSD([sQuery(id+"F2.wireOp",EDGE,"E5.left")])]})])],"derivedFrom":makeQuery(id+"F7.opExtrude","SWEPT_FACE",FACE,{"disambiguationData":[OSD([sQuery(id+"F6.wireOp",EDGE,"E33.MirrorCS")])]})}),makeQuery(id+"F9.opExtrude","SWEPT_FACE",FACE,{"disambiguationData":[OSD([sQuery(id+"F8.wireOp",EDGE,"E43.0.1.3")])]})]});
            var Q94;
            {var subQ0=sQuery(id+"F2.wireOp",EDGE,"E5.right");Q94=makeQuery(id+"F7.boolean.opBoolean","SPLIT",EDGE,{"disambiguationData":[TD([makeQuery(id+"F7.opExtrude","SWEPT_FACE",FACE,{"disambiguationData":[OSD([sQuery(id+"F6.wireOp",EDGE,"E22.MirrorCS")])]})])],"derivedFrom":makeQuery(id+"F3.opExtrude","CAP_EDGE",EDGE,{"disambiguationData":[OSD([subQ0])],"isStart":false})});}
            var Q95;
            Q95=makeQuery(id+"F9.boolean.opBoolean","INTERSECT",EDGE,{"derivedFrom":[makeQuery(id+"F7.boolean.opBoolean","COPY",FACE,{"disambiguationData":[TD([makeQuery(id+"F3.opExtrude","SWEPT_FACE",FACE,{"disambiguationData":[OSD([sQuery(id+"F2.wireOp",EDGE,"E5.left")])]})])],"derivedFrom":makeQuery(id+"F7.opExtrude","SWEPT_FACE",FACE,{"disambiguationData":[OSD([sQuery(id+"F6.wireOp",EDGE,"E41.MirrorCS")])]})}),makeQuery(id+"F9.opExtrude","SWEPT_FACE",FACE,{"disambiguationData":[OSD([sQuery(id+"F8.wireOp",EDGE,"E43.0.2.3")])]})]});
            var Q96;
            {var subQ0=sQuery(id+"F2.wireOp",EDGE,"E5.right");Q96=makeQuery(id+"F7.boolean.opBoolean","SPLIT",EDGE,{"disambiguationData":[TD([makeQuery(id+"F7.opExtrude","SWEPT_FACE",FACE,{"disambiguationData":[OSD([sQuery(id+"F6.wireOp",EDGE,"E25.MirrorCS")])]})])],"derivedFrom":makeQuery(id+"F3.opExtrude","CAP_EDGE",EDGE,{"disambiguationData":[OSD([subQ0])],"isStart":false})});}
            var Q97;
            Q97=makeQuery(id+"F9.boolean.opBoolean","INTERSECT",EDGE,{"derivedFrom":[makeQuery(id+"F7.boolean.opBoolean","COPY",FACE,{"disambiguationData":[TD([makeQuery(id+"F3.opExtrude","SWEPT_FACE",FACE,{"disambiguationData":[OSD([sQuery(id+"F2.wireOp",EDGE,"E5.left")])]})])],"derivedFrom":makeQuery(id+"F7.opExtrude","SWEPT_FACE",FACE,{"disambiguationData":[OSD([sQuery(id+"F6.wireOp",EDGE,"E40.MirrorCS")])]})}),makeQuery(id+"F9.opExtrude","SWEPT_FACE",FACE,{"disambiguationData":[OSD([sQuery(id+"F8.wireOp",EDGE,"E43.0.3.3")])]})]});
            var Q98;
            {var subQ0=sQuery(id+"F2.wireOp",EDGE,"E5.right");Q98=makeQuery(id+"F7.boolean.opBoolean","SPLIT",EDGE,{"disambiguationData":[TD([makeQuery(id+"F7.opExtrude","SWEPT_FACE",FACE,{"disambiguationData":[OSD([sQuery(id+"F6.wireOp",EDGE,"E24.MirrorCS")])]})])],"derivedFrom":makeQuery(id+"F3.opExtrude","CAP_EDGE",EDGE,{"disambiguationData":[OSD([subQ0])],"isStart":false})});}
            var Q99;
            Q99=makeQuery(id+"F9.boolean.opBoolean","INTERSECT",EDGE,{"derivedFrom":[makeQuery(id+"F7.boolean.opBoolean","COPY",FACE,{"disambiguationData":[TD([makeQuery(id+"F3.opExtrude","SWEPT_FACE",FACE,{"disambiguationData":[OSD([sQuery(id+"F2.wireOp",EDGE,"E5.left")])]})])],"derivedFrom":makeQuery(id+"F7.opExtrude","SWEPT_FACE",FACE,{"disambiguationData":[OSD([sQuery(id+"F6.wireOp",EDGE,"E32.MirrorCS")])]})}),makeQuery(id+"F9.opExtrude","SWEPT_FACE",FACE,{"disambiguationData":[OSD([sQuery(id+"F8.wireOp",EDGE,"E43.0.4.3")])]})]});
            var Q100;
            {var subQ0=sQuery(id+"F2.wireOp",EDGE,"E5.right");var subQ1=sQuery(id+"F2.wireOp",EDGE,"E5.top");Q100=makeQuery(id+"F7.boolean.opBoolean","SPLIT",EDGE,{"disambiguationData":[TD([makeQuery(id+"F3.opExtrude","SWEPT_FACE",FACE,{"disambiguationData":[OSD([subQ1])]})])],"derivedFrom":makeQuery(id+"F3.opExtrude","CAP_EDGE",EDGE,{"disambiguationData":[OSD([subQ0])],"isStart":false})});}
            var Q101;
            {var subQ0=sQuery(id+"F2.wireOp",EDGE,"E5.bottom");var subQ1=sQuery(id+"F2.wireOp",EDGE,"E5.right");Q101=makeQuery(id+"F7.boolean.opBoolean","SPLIT",EDGE,{"disambiguationData":[TD([makeQuery(id+"F3.opExtrude","SWEPT_FACE",FACE,{"disambiguationData":[OSD([subQ0])]})])],"derivedFrom":makeQuery(id+"F3.opExtrude","CAP_EDGE",EDGE,{"disambiguationData":[OSD([subQ1])],"isStart":true})});}
            var Q102;
            Q102=makeQuery(id+"F9.boolean.opBoolean","INTERSECT",EDGE,{"derivedFrom":[makeQuery(id+"F7.boolean.opBoolean","COPY",FACE,{"disambiguationData":[TD([makeQuery(id+"F3.opExtrude","SWEPT_FACE",FACE,{"disambiguationData":[OSD([sQuery(id+"F2.wireOp",EDGE,"E5.left")])]})])],"derivedFrom":makeQuery(id+"F7.opExtrude","SWEPT_FACE",FACE,{"disambiguationData":[OSD([sQuery(id+"F6.wireOp",EDGE,"E14.4.0.1")])]})}),makeQuery(id+"F9.opExtrude","SWEPT_FACE",FACE,{"disambiguationData":[OSD([sQuery(id+"F8.wireOp",EDGE,"E42.left")])]})]});
            var Q103;
            {var subQ0=sQuery(id+"F2.wireOp",EDGE,"E5.right");Q103=makeQuery(id+"F7.boolean.opBoolean","SPLIT",EDGE,{"disambiguationData":[TD([makeQuery(id+"F7.opExtrude","SWEPT_FACE",FACE,{"disambiguationData":[OSD([sQuery(id+"F6.wireOp",EDGE,"E14.3.0.0")])]})])],"derivedFrom":makeQuery(id+"F3.opExtrude","CAP_EDGE",EDGE,{"disambiguationData":[OSD([subQ0])],"isStart":true})});}
            var Q104;
            Q104=makeQuery(id+"F9.boolean.opBoolean","INTERSECT",EDGE,{"derivedFrom":[makeQuery(id+"F7.boolean.opBoolean","COPY",FACE,{"disambiguationData":[TD([makeQuery(id+"F3.opExtrude","SWEPT_FACE",FACE,{"disambiguationData":[OSD([sQuery(id+"F2.wireOp",EDGE,"E5.left")])]})])],"derivedFrom":makeQuery(id+"F7.opExtrude","SWEPT_FACE",FACE,{"disambiguationData":[OSD([sQuery(id+"F6.wireOp",EDGE,"E14.3.0.1")])]})}),makeQuery(id+"F9.opExtrude","SWEPT_FACE",FACE,{"disambiguationData":[OSD([sQuery(id+"F8.wireOp",EDGE,"E43.0.1.3")])]})]});
            var Q105;
            {var subQ0=sQuery(id+"F2.wireOp",EDGE,"E5.right");Q105=makeQuery(id+"F7.boolean.opBoolean","SPLIT",EDGE,{"disambiguationData":[TD([makeQuery(id+"F7.opExtrude","SWEPT_FACE",FACE,{"disambiguationData":[OSD([sQuery(id+"F6.wireOp",EDGE,"E14.2.0.0")])]})])],"derivedFrom":makeQuery(id+"F3.opExtrude","CAP_EDGE",EDGE,{"disambiguationData":[OSD([subQ0])],"isStart":true})});}
            var Q106;
            Q106=makeQuery(id+"F9.boolean.opBoolean","INTERSECT",EDGE,{"derivedFrom":[makeQuery(id+"F7.boolean.opBoolean","COPY",FACE,{"disambiguationData":[TD([makeQuery(id+"F3.opExtrude","SWEPT_FACE",FACE,{"disambiguationData":[OSD([sQuery(id+"F2.wireOp",EDGE,"E5.left")])]})])],"derivedFrom":makeQuery(id+"F7.opExtrude","SWEPT_FACE",FACE,{"disambiguationData":[OSD([sQuery(id+"F6.wireOp",EDGE,"E14.2.0.1")])]})}),makeQuery(id+"F9.opExtrude","SWEPT_FACE",FACE,{"disambiguationData":[OSD([sQuery(id+"F8.wireOp",EDGE,"E43.0.2.3")])]})]});
            var Q107;
            {var subQ0=sQuery(id+"F2.wireOp",EDGE,"E5.right");Q107=makeQuery(id+"F7.boolean.opBoolean","SPLIT",EDGE,{"disambiguationData":[TD([makeQuery(id+"F7.opExtrude","SWEPT_FACE",FACE,{"disambiguationData":[OSD([sQuery(id+"F6.wireOp",EDGE,"E14.1.0.0")])]})])],"derivedFrom":makeQuery(id+"F3.opExtrude","CAP_EDGE",EDGE,{"disambiguationData":[OSD([subQ0])],"isStart":true})});}
            var Q108;
            Q108=makeQuery(id+"F9.boolean.opBoolean","INTERSECT",EDGE,{"derivedFrom":[makeQuery(id+"F7.boolean.opBoolean","COPY",FACE,{"disambiguationData":[TD([makeQuery(id+"F3.opExtrude","SWEPT_FACE",FACE,{"disambiguationData":[OSD([sQuery(id+"F2.wireOp",EDGE,"E5.left")])]})])],"derivedFrom":makeQuery(id+"F7.opExtrude","SWEPT_FACE",FACE,{"disambiguationData":[OSD([sQuery(id+"F6.wireOp",EDGE,"E14.1.0.1")])]})}),makeQuery(id+"F9.opExtrude","SWEPT_FACE",FACE,{"disambiguationData":[OSD([sQuery(id+"F8.wireOp",EDGE,"E43.0.3.3")])]})]});
            var Q109;
            {var subQ0=sQuery(id+"F2.wireOp",EDGE,"E5.right");Q109=makeQuery(id+"F7.boolean.opBoolean","SPLIT",EDGE,{"disambiguationData":[TD([makeQuery(id+"F7.opExtrude","SWEPT_FACE",FACE,{"disambiguationData":[OSD([sQuery(id+"F6.wireOp",EDGE,"E13")])]})])],"derivedFrom":makeQuery(id+"F3.opExtrude","CAP_EDGE",EDGE,{"disambiguationData":[OSD([subQ0])],"isStart":true})});}
            var Q110;
            Q110=makeQuery(id+"F9.boolean.opBoolean","INTERSECT",EDGE,{"derivedFrom":[makeQuery(id+"F7.boolean.opBoolean","COPY",FACE,{"disambiguationData":[TD([makeQuery(id+"F3.opExtrude","SWEPT_FACE",FACE,{"disambiguationData":[OSD([sQuery(id+"F2.wireOp",EDGE,"E5.left")])]})])],"derivedFrom":makeQuery(id+"F7.opExtrude","SWEPT_FACE",FACE,{"disambiguationData":[OSD([sQuery(id+"F6.wireOp",EDGE,"E12")])]})}),makeQuery(id+"F9.opExtrude","SWEPT_FACE",FACE,{"disambiguationData":[OSD([sQuery(id+"F8.wireOp",EDGE,"E43.0.4.3")])]})]});
            var Q111;
            {var subQ0=sQuery(id+"F2.wireOp",EDGE,"E5.right");var subQ1=sQuery(id+"F2.wireOp",EDGE,"E5.top");Q111=makeQuery(id+"F7.boolean.opBoolean","SPLIT",EDGE,{"disambiguationData":[TD([makeQuery(id+"F3.opExtrude","SWEPT_FACE",FACE,{"disambiguationData":[OSD([subQ1])]})])],"derivedFrom":makeQuery(id+"F3.opExtrude","CAP_EDGE",EDGE,{"disambiguationData":[OSD([subQ0])],"isStart":true})});}
            var Q112;
            {var subQ0=sQuery(id+"F2.wireOp",EDGE,"E6.bottom");var subQ1=sQuery(id+"F2.wireOp",EDGE,"E6.left");Q112=makeQuery(id+"F7.boolean.opBoolean","SPLIT",EDGE,{"disambiguationData":[TD([makeQuery(id+"F3.opExtrude","SWEPT_FACE",FACE,{"disambiguationData":[OSD([subQ0])]})])],"derivedFrom":makeQuery(id+"F3.opExtrude","CAP_EDGE",EDGE,{"disambiguationData":[OSD([subQ1])],"isStart":true})});}
            var Q113;
            {var subQ0=sQuery(id+"F2.wireOp",EDGE,"E6.left");Q113=makeQuery(id+"F7.boolean.opBoolean","SPLIT",EDGE,{"disambiguationData":[TD([makeQuery(id+"F7.opExtrude","SWEPT_FACE",FACE,{"disambiguationData":[OSD([sQuery(id+"F6.wireOp",EDGE,"E14.3.0.0")])]})])],"derivedFrom":makeQuery(id+"F3.opExtrude","CAP_EDGE",EDGE,{"disambiguationData":[OSD([subQ0])],"isStart":true})});}
            var Q114;
            {var subQ0=sQuery(id+"F2.wireOp",EDGE,"E6.left");Q114=makeQuery(id+"F7.boolean.opBoolean","SPLIT",EDGE,{"disambiguationData":[TD([makeQuery(id+"F7.opExtrude","SWEPT_FACE",FACE,{"disambiguationData":[OSD([sQuery(id+"F6.wireOp",EDGE,"E14.2.0.0")])]})])],"derivedFrom":makeQuery(id+"F3.opExtrude","CAP_EDGE",EDGE,{"disambiguationData":[OSD([subQ0])],"isStart":true})});}
            var Q115;
            Q115=makeQuery(id+"F7.boolean.opBoolean","INTERSECT",EDGE,{"derivedFrom":[makeQuery(id+"F3.opExtrude","SWEPT_FACE",FACE,{"disambiguationData":[OSD([sQuery(id+"F2.wireOp",EDGE,"E6.left")])]}),makeQuery(id+"F7.opExtrude","SWEPT_FACE",FACE,{"disambiguationData":[OSD([sQuery(id+"F6.wireOp",EDGE,"E14.3.0.1")])]})]});
            var Q116;
            Q116=makeQuery(id+"F7.boolean.opBoolean","INTERSECT",EDGE,{"derivedFrom":[makeQuery(id+"F3.opExtrude","SWEPT_FACE",FACE,{"disambiguationData":[OSD([sQuery(id+"F2.wireOp",EDGE,"E6.left")])]}),makeQuery(id+"F7.opExtrude","SWEPT_FACE",FACE,{"disambiguationData":[OSD([sQuery(id+"F6.wireOp",EDGE,"E14.4.0.1")])]})]});
            var Q117;
            Q117=makeQuery(id+"F7.boolean.opBoolean","INTERSECT",EDGE,{"derivedFrom":[makeQuery(id+"F3.opExtrude","SWEPT_FACE",FACE,{"disambiguationData":[OSD([sQuery(id+"F2.wireOp",EDGE,"E6.left")])]}),makeQuery(id+"F7.opExtrude","SWEPT_FACE",FACE,{"disambiguationData":[OSD([sQuery(id+"F6.wireOp",EDGE,"E14.2.0.1")])]})]});
            var Q118;
            {var subQ0=sQuery(id+"F2.wireOp",EDGE,"E6.left");Q118=makeQuery(id+"F7.boolean.opBoolean","SPLIT",EDGE,{"disambiguationData":[TD([makeQuery(id+"F7.opExtrude","SWEPT_FACE",FACE,{"disambiguationData":[OSD([sQuery(id+"F6.wireOp",EDGE,"E14.1.0.0")])]})])],"derivedFrom":makeQuery(id+"F3.opExtrude","CAP_EDGE",EDGE,{"disambiguationData":[OSD([subQ0])],"isStart":true})});}
            var Q119;
            Q119=makeQuery(id+"F7.boolean.opBoolean","INTERSECT",EDGE,{"derivedFrom":[makeQuery(id+"F3.opExtrude","SWEPT_FACE",FACE,{"disambiguationData":[OSD([sQuery(id+"F2.wireOp",EDGE,"E6.left")])]}),makeQuery(id+"F7.opExtrude","SWEPT_FACE",FACE,{"disambiguationData":[OSD([sQuery(id+"F6.wireOp",EDGE,"E14.1.0.1")])]})]});
            var Q120;
            {var subQ0=sQuery(id+"F2.wireOp",EDGE,"E6.left");Q120=makeQuery(id+"F7.boolean.opBoolean","SPLIT",EDGE,{"disambiguationData":[TD([makeQuery(id+"F7.opExtrude","SWEPT_FACE",FACE,{"disambiguationData":[OSD([sQuery(id+"F6.wireOp",EDGE,"E13")])]})])],"derivedFrom":makeQuery(id+"F3.opExtrude","CAP_EDGE",EDGE,{"disambiguationData":[OSD([subQ0])],"isStart":true})});}
            var Q121;
            Q121=makeQuery(id+"F7.boolean.opBoolean","INTERSECT",EDGE,{"derivedFrom":[makeQuery(id+"F3.opExtrude","SWEPT_FACE",FACE,{"disambiguationData":[OSD([sQuery(id+"F2.wireOp",EDGE,"E6.left")])]}),makeQuery(id+"F7.opExtrude","SWEPT_FACE",FACE,{"disambiguationData":[OSD([sQuery(id+"F6.wireOp",EDGE,"E12")])]})]});
            var Q122;
            {var subQ0=sQuery(id+"F2.wireOp",EDGE,"E6.left");var subQ1=sQuery(id+"F2.wireOp",EDGE,"E6.top");Q122=makeQuery(id+"F7.boolean.opBoolean","SPLIT",EDGE,{"disambiguationData":[TD([makeQuery(id+"F3.opExtrude","SWEPT_FACE",FACE,{"disambiguationData":[OSD([subQ1])]})])],"derivedFrom":makeQuery(id+"F3.opExtrude","CAP_EDGE",EDGE,{"disambiguationData":[OSD([subQ0])],"isStart":true})});}
            var Q123;
            Q123=makeQuery(id+"F1.opExtrude","SWEPT_EDGE",EDGE,{"disambiguationData":[OSD([sQuery(id+"F0.wireOp",EDGE,"E0.bottom"),sQuery(id+"F0.wireOp",EDGE,"E0.right")])]});
            var Q124;
            {var subQ0=sQuery(id+"F2.wireOp",EDGE,"E5.bottom");var subQ1=sQuery(id+"F2.wireOp",EDGE,"E5.left");Q124=makeQuery(id+"F7.boolean.opBoolean","SPLIT",EDGE,{"disambiguationData":[TD([makeQuery(id+"F3.opExtrude","SWEPT_FACE",FACE,{"disambiguationData":[OSD([subQ0])]})])],"derivedFrom":makeQuery(id+"F3.opExtrude","CAP_EDGE",EDGE,{"disambiguationData":[OSD([subQ1])],"isStart":true})});}
            var Q125;
            {var subQ0=sQuery(id+"F2.wireOp",EDGE,"E5.left");Q125=makeQuery(id+"F7.boolean.opBoolean","SPLIT",EDGE,{"disambiguationData":[TD([makeQuery(id+"F7.opExtrude","SWEPT_FACE",FACE,{"disambiguationData":[OSD([sQuery(id+"F6.wireOp",EDGE,"E14.3.0.0")])]})])],"derivedFrom":makeQuery(id+"F3.opExtrude","CAP_EDGE",EDGE,{"disambiguationData":[OSD([subQ0])],"isStart":true})});}
            var Q126;
            {var subQ0=sQuery(id+"F2.wireOp",EDGE,"E5.left");Q126=makeQuery(id+"F7.boolean.opBoolean","SPLIT",EDGE,{"disambiguationData":[TD([makeQuery(id+"F7.opExtrude","SWEPT_FACE",FACE,{"disambiguationData":[OSD([sQuery(id+"F6.wireOp",EDGE,"E14.2.0.0")])]})])],"derivedFrom":makeQuery(id+"F3.opExtrude","CAP_EDGE",EDGE,{"disambiguationData":[OSD([subQ0])],"isStart":true})});}
            var Q127;
            {var subQ0=sQuery(id+"F2.wireOp",EDGE,"E5.left");Q127=makeQuery(id+"F7.boolean.opBoolean","SPLIT",EDGE,{"disambiguationData":[TD([makeQuery(id+"F7.opExtrude","SWEPT_FACE",FACE,{"disambiguationData":[OSD([sQuery(id+"F6.wireOp",EDGE,"E14.1.0.0")])]})])],"derivedFrom":makeQuery(id+"F3.opExtrude","CAP_EDGE",EDGE,{"disambiguationData":[OSD([subQ0])],"isStart":true})});}
            var Q128;
            {var subQ0=sQuery(id+"F2.wireOp",EDGE,"E5.left");Q128=makeQuery(id+"F7.boolean.opBoolean","SPLIT",EDGE,{"disambiguationData":[TD([makeQuery(id+"F7.opExtrude","SWEPT_FACE",FACE,{"disambiguationData":[OSD([sQuery(id+"F6.wireOp",EDGE,"E13")])]})])],"derivedFrom":makeQuery(id+"F3.opExtrude","CAP_EDGE",EDGE,{"disambiguationData":[OSD([subQ0])],"isStart":true})});}
            var Q129;
            {var subQ0=sQuery(id+"F2.wireOp",EDGE,"E5.left");var subQ1=sQuery(id+"F2.wireOp",EDGE,"E5.top");Q129=makeQuery(id+"F7.boolean.opBoolean","SPLIT",EDGE,{"disambiguationData":[TD([makeQuery(id+"F3.opExtrude","SWEPT_FACE",FACE,{"disambiguationData":[OSD([subQ1])]})])],"derivedFrom":makeQuery(id+"F3.opExtrude","CAP_EDGE",EDGE,{"disambiguationData":[OSD([subQ0])],"isStart":true})});}
            var Q130;
            Q130=makeQuery(id+"F1.opExtrude","SWEPT_EDGE",EDGE,{"disambiguationData":[OSD([sQuery(id+"F0.wireOp",EDGE,"E0.bottom"),sQuery(id+"F0.wireOp",EDGE,"E0.left")])]});
            var Q131;
            Q131=makeQuery(id+"F7.boolean.opBoolean","INTERSECT",EDGE,{"derivedFrom":[makeQuery(id+"F3.opExtrude","SWEPT_FACE",FACE,{"disambiguationData":[OSD([sQuery(id+"F2.wireOp",EDGE,"E5.left")])]}),makeQuery(id+"F7.opExtrude","SWEPT_FACE",FACE,{"disambiguationData":[OSD([sQuery(id+"F6.wireOp",EDGE,"E12")])]})]});
            var Q132;
            Q132=makeQuery(id+"F7.boolean.opBoolean","INTERSECT",EDGE,{"derivedFrom":[makeQuery(id+"F3.opExtrude","SWEPT_FACE",FACE,{"disambiguationData":[OSD([sQuery(id+"F2.wireOp",EDGE,"E5.left")])]}),makeQuery(id+"F7.opExtrude","SWEPT_FACE",FACE,{"disambiguationData":[OSD([sQuery(id+"F6.wireOp",EDGE,"E14.1.0.1")])]})]});
            var Q133;
            Q133=makeQuery(id+"F7.boolean.opBoolean","INTERSECT",EDGE,{"derivedFrom":[makeQuery(id+"F3.opExtrude","SWEPT_FACE",FACE,{"disambiguationData":[OSD([sQuery(id+"F2.wireOp",EDGE,"E5.left")])]}),makeQuery(id+"F7.opExtrude","SWEPT_FACE",FACE,{"disambiguationData":[OSD([sQuery(id+"F6.wireOp",EDGE,"E14.2.0.1")])]})]});
            var Q134;
            Q134=makeQuery(id+"F7.boolean.opBoolean","INTERSECT",EDGE,{"derivedFrom":[makeQuery(id+"F3.opExtrude","SWEPT_FACE",FACE,{"disambiguationData":[OSD([sQuery(id+"F2.wireOp",EDGE,"E5.left")])]}),makeQuery(id+"F7.opExtrude","SWEPT_FACE",FACE,{"disambiguationData":[OSD([sQuery(id+"F6.wireOp",EDGE,"E14.3.0.1")])]})]});
            var Q135;
            Q135=makeQuery(id+"F7.boolean.opBoolean","INTERSECT",EDGE,{"derivedFrom":[makeQuery(id+"F3.opExtrude","SWEPT_FACE",FACE,{"disambiguationData":[OSD([sQuery(id+"F2.wireOp",EDGE,"E5.left")])]}),makeQuery(id+"F7.opExtrude","SWEPT_FACE",FACE,{"disambiguationData":[OSD([sQuery(id+"F6.wireOp",EDGE,"E14.4.0.1")])]})]});
            fillet(context, id + "F13", {"entities" : qUnion([Q0, Q1, Q2, Q3, Q4, Q5, Q6, Q7, Q8, Q9, Q10, Q11, Q12, Q13, Q14, Q15, Q16, Q17, Q18, Q19, Q20, Q21, Q22, Q23, Q24, Q25, Q26, Q27, Q28, Q29, Q30, Q31, Q32, Q33, Q34, Q35, Q36, Q37, Q38, Q39, Q40, Q41, Q42, Q43, Q44, Q45, Q46, Q47, Q48, Q49, Q50, Q51, Q52, Q53, Q54, Q55, Q56, Q57, Q58, Q59, Q60, Q61, Q62, Q63, Q64, Q65, Q66, Q67, Q68, Q69, Q70, Q71, Q72, Q73, Q74, Q75, Q76, Q77, Q78, Q79, Q80, Q81, Q82, Q83, Q84, Q85, Q86, Q87, Q88, Q89, Q90, Q91, Q92, Q93, Q94, Q95, Q96, Q97, Q98, Q99, Q100, Q101, Q102, Q103, Q104, Q105, Q106, Q107, Q108, Q109, Q110, Q111, Q112, Q113, Q114, Q115, Q116, Q117, Q118, Q119, Q120, Q121, Q122, Q123, Q124, Q125, Q126, Q127, Q128, Q129, Q130, Q131, Q132, Q133, Q134, Q135]), "radius" : 2 * mm, "tangentPropagation" : true, "allowEdgeOverflow" : false});
        }
        {
            var Q0;
            Q0=makeQuery(id+"F1.opExtrude","SWEPT_FACE",FACE,{"disambiguationData":[OSD([sQuery(id+"F0.wireOp",EDGE,"E0.top")])]});
            var sketch = newSketch(context, id + "F14", { "sketchPlane" : qUnion([Q0])});
            skLineSegment(sketch, "E68.0", {"start": v(-2548, 90) * mm, "end": v(-2548, 82) * mm});
            skPoint(sketch, "E69.0", {"position": v(-2550, 10) * mm});
            skPoint(sketch, "E69.1", {"position": v(-2550, 18) * mm});
            skPoint(sketch, "E69.2", {"position": v(-2550, 28) * mm});
            skPoint(sketch, "E69.3", {"position": v(-2550, 36) * mm});
            skPoint(sketch, "E69.4", {"position": v(-2550, 46) * mm});
            skPoint(sketch, "E69.5", {"position": v(-2550, 54) * mm});
            skPoint(sketch, "E69.6", {"position": v(-2550, 64) * mm});
            skPoint(sketch, "E69.7", {"position": v(-2550, 72) * mm});
            skPoint(sketch, "E69.8", {"position": v(-2550, 82) * mm});
            skPoint(sketch, "E69.9", {"position": v(-2550, 90) * mm});
            skLineSegment(sketch, "E70", {"start": v(-2550, 10) * mm, "end": v(-2548, 10) * mm});
            skLineSegment(sketch, "E71", {"start": v(-2548, 18) * mm, "end": v(-2550, 18) * mm});
            skLineSegment(sketch, "E72", {"start": v(-2550, 28) * mm, "end": v(-2548, 28) * mm});
            skLineSegment(sketch, "E73", {"start": v(-2548, 36) * mm, "end": v(-2550, 36) * mm});
            skLineSegment(sketch, "E74", {"start": v(-2550, 46) * mm, "end": v(-2548, 46) * mm});
            skLineSegment(sketch, "E75", {"start": v(-2548, 54) * mm, "end": v(-2550, 54) * mm});
            skLineSegment(sketch, "E76", {"start": v(-2550, 64) * mm, "end": v(-2548, 64) * mm});
            skLineSegment(sketch, "E77", {"start": v(-2548, 72) * mm, "end": v(-2550, 72) * mm});
            skLineSegment(sketch, "E78", {"start": v(-2550, 82) * mm, "end": v(-2548, 82) * mm});
            skLineSegment(sketch, "E79", {"start": v(-2548, 90) * mm, "end": v(-2550, 90) * mm});
            skLineSegment(sketch, "E80.trimOffspring", {"start": v(-2548, 18) * mm, "end": v(-2548, 10) * mm});
            skLineSegment(sketch, "E81.trimOffspring", {"start": v(-2548, 36) * mm, "end": v(-2548, 28) * mm});
            skLineSegment(sketch, "E82.trimOffspring", {"start": v(-2548, 54) * mm, "end": v(-2548, 46) * mm});
            skLineSegment(sketch, "E83.trimOffspring", {"start": v(-2548, 72) * mm, "end": v(-2548, 64) * mm});
            skLineSegment(sketch, "E84", {"start": v(-2525, 0) * mm, "end": v(-2525, 100) * mm, "construction": true});
            skLineSegment(sketch, "E85", {"start": v(-2550, 10) * mm, "end": v(-2550, 18) * mm});
            skLineSegment(sketch, "E86", {"start": v(-2550, 28) * mm, "end": v(-2550, 36) * mm});
            skLineSegment(sketch, "E87", {"start": v(-2550, 46) * mm, "end": v(-2550, 54) * mm});
            skLineSegment(sketch, "E88", {"start": v(-2550, 64) * mm, "end": v(-2550, 72) * mm});
            skLineSegment(sketch, "E89", {"start": v(-2550, 82) * mm, "end": v(-2550, 90) * mm});
            skLineSegment(sketch, "E90.MirrorCS", {"start": v(-2500, 28) * mm, "end": v(-2502, 28) * mm});
            skLineSegment(sketch, "E91.MirrorCS", {"start": v(-2502, 36) * mm, "end": v(-2500, 36) * mm});
            skLineSegment(sketch, "E92.MirrorCS", {"start": v(-2502, 54) * mm, "end": v(-2500, 54) * mm});
            skLineSegment(sketch, "E93.MirrorCS", {"start": v(-2502, 18) * mm, "end": v(-2500, 18) * mm});
            skLineSegment(sketch, "E94.MirrorCS", {"start": v(-2500, 82) * mm, "end": v(-2502, 82) * mm});
            skLineSegment(sketch, "E95.MirrorCS", {"start": v(-2500, 10) * mm, "end": v(-2502, 10) * mm});
            skLineSegment(sketch, "E96.MirrorCS", {"start": v(-2500, 46) * mm, "end": v(-2502, 46) * mm});
            skLineSegment(sketch, "E97.MirrorCS", {"start": v(-2500, 64) * mm, "end": v(-2502, 64) * mm});
            skLineSegment(sketch, "E98.MirrorCS", {"start": v(-2502, 72) * mm, "end": v(-2500, 72) * mm});
            skLineSegment(sketch, "E99.MirrorCS", {"start": v(-2502, 90) * mm, "end": v(-2500, 90) * mm});
            skPoint(sketch, "E100.MirrorP", {"position": v(-2500, 46) * mm});
            skPoint(sketch, "E101.MirrorP", {"position": v(-2500, 10) * mm});
            skLineSegment(sketch, "E102.MirrorCS", {"start": v(-2500, 64) * mm, "end": v(-2500, 72) * mm});
            skLineSegment(sketch, "E103.MirrorCS", {"start": v(-2502, 90) * mm, "end": v(-2502, 82) * mm});
            skLineSegment(sketch, "E104.MirrorCS", {"start": v(-2502, 72) * mm, "end": v(-2502, 64) * mm});
            skLineSegment(sketch, "E105.MirrorCS", {"start": v(-2502, 54) * mm, "end": v(-2502, 46) * mm});
            skPoint(sketch, "E106.MirrorP", {"position": v(-2500, 18) * mm});
            skLineSegment(sketch, "E107.MirrorCS", {"start": v(-2500, 82) * mm, "end": v(-2500, 90) * mm});
            skLineSegment(sketch, "E108.MirrorCS", {"start": v(-2500, 28) * mm, "end": v(-2500, 36) * mm});
            skPoint(sketch, "E109.MirrorP", {"position": v(-2500, 28) * mm});
            skPoint(sketch, "E110.MirrorP", {"position": v(-2500, 64) * mm});
            skLineSegment(sketch, "E111.MirrorCS", {"start": v(-2502, 18) * mm, "end": v(-2502, 10) * mm});
            skLineSegment(sketch, "E112.MirrorCS", {"start": v(-2500, 10) * mm, "end": v(-2500, 18) * mm});
            skPoint(sketch, "E113.MirrorP", {"position": v(-2500, 82) * mm});
            skPoint(sketch, "E114.MirrorP", {"position": v(-2500, 90) * mm});
            skPoint(sketch, "E115.MirrorP", {"position": v(-2500, 36) * mm});
            skPoint(sketch, "E116.MirrorP", {"position": v(-2500, 54) * mm});
            skLineSegment(sketch, "E117.MirrorCS", {"start": v(-2500, 46) * mm, "end": v(-2500, 54) * mm});
            skLineSegment(sketch, "E118.MirrorCS", {"start": v(-2502, 36) * mm, "end": v(-2502, 28) * mm});
            skPoint(sketch, "E119.MirrorP", {"position": v(-2500, 72) * mm});
            skLineSegment(sketch, "E120.MirrorCS", {"start": v(2500, 46) * mm, "end": v(2502, 46) * mm});
            skLineSegment(sketch, "E121.MirrorCS", {"start": v(2502, 54) * mm, "end": v(2500, 54) * mm});
            skLineSegment(sketch, "E122.MirrorCS", {"start": v(2500, 82) * mm, "end": v(2502, 82) * mm});
            skLineSegment(sketch, "E123.MirrorCS", {"start": v(2502, 36) * mm, "end": v(2500, 36) * mm});
            skLineSegment(sketch, "E124.MirrorCS", {"start": v(2502, 72) * mm, "end": v(2500, 72) * mm});
            skLineSegment(sketch, "E125.MirrorCS", {"start": v(2500, 64) * mm, "end": v(2502, 64) * mm});
            skLineSegment(sketch, "E126.MirrorCS", {"start": v(2502, 18) * mm, "end": v(2500, 18) * mm});
            skLineSegment(sketch, "E127.MirrorCS", {"start": v(2500, 10) * mm, "end": v(2502, 10) * mm});
            skLineSegment(sketch, "E128.MirrorCS", {"start": v(2500, 28) * mm, "end": v(2502, 28) * mm});
            skLineSegment(sketch, "E129.MirrorCS", {"start": v(2502, 90) * mm, "end": v(2500, 90) * mm});
            skLineSegment(sketch, "E130.MirrorCS", {"start": v(2548, 72) * mm, "end": v(2550, 72) * mm});
            skLineSegment(sketch, "E131.MirrorCS", {"start": v(2550, 10) * mm, "end": v(2548, 10) * mm});
            skLineSegment(sketch, "E132.MirrorCS", {"start": v(2550, 64) * mm, "end": v(2548, 64) * mm});
            skLineSegment(sketch, "E133.MirrorCS", {"start": v(2548, 18) * mm, "end": v(2550, 18) * mm});
            skLineSegment(sketch, "E134.MirrorCS", {"start": v(2548, 54) * mm, "end": v(2550, 54) * mm});
            skLineSegment(sketch, "E135.MirrorCS", {"start": v(2550, 28) * mm, "end": v(2548, 28) * mm});
            skLineSegment(sketch, "E136.MirrorCS", {"start": v(2548, 90) * mm, "end": v(2550, 90) * mm});
            skLineSegment(sketch, "E137.MirrorCS", {"start": v(2548, 36) * mm, "end": v(2550, 36) * mm});
            skLineSegment(sketch, "E138.MirrorCS", {"start": v(2550, 82) * mm, "end": v(2548, 82) * mm});
            skLineSegment(sketch, "E139.MirrorCS", {"start": v(2550, 46) * mm, "end": v(2548, 46) * mm});
            skLineSegment(sketch, "E140.MirrorCS", {"start": v(2550, 46) * mm, "end": v(2550, 54) * mm});
            skLineSegment(sketch, "E141.MirrorCS", {"start": v(2548, 54) * mm, "end": v(2548, 46) * mm});
            skPoint(sketch, "E142.MirrorP", {"position": v(2550, 10) * mm});
            skPoint(sketch, "E143.MirrorP", {"position": v(2500, 90) * mm});
            skPoint(sketch, "E144.MirrorP", {"position": v(2500, 36) * mm});
            skLineSegment(sketch, "E145.MirrorCS", {"start": v(2550, 64) * mm, "end": v(2550, 72) * mm});
            skPoint(sketch, "E146.MirrorP", {"position": v(2550, 82) * mm});
            skPoint(sketch, "E147.MirrorP", {"position": v(2550, 54) * mm});
            skLineSegment(sketch, "E148.MirrorCS", {"start": v(2550, 10) * mm, "end": v(2550, 18) * mm});
            skPoint(sketch, "E149.MirrorP", {"position": v(2500, 82) * mm});
            skLineSegment(sketch, "E150.MirrorCS", {"start": v(2500, 64) * mm, "end": v(2500, 72) * mm});
            skLineSegment(sketch, "E151.MirrorCS", {"start": v(2500, 10) * mm, "end": v(2500, 18) * mm});
            skLineSegment(sketch, "E152.MirrorCS", {"start": v(2548, 36) * mm, "end": v(2548, 28) * mm});
            skLineSegment(sketch, "E153.MirrorCS", {"start": v(2502, 90) * mm, "end": v(2502, 82) * mm});
            skPoint(sketch, "E154.MirrorP", {"position": v(2550, 90) * mm});
            skLineSegment(sketch, "E155.MirrorCS", {"start": v(2500, 28) * mm, "end": v(2500, 36) * mm});
            skPoint(sketch, "E156.MirrorP", {"position": v(2550, 46) * mm});
            skPoint(sketch, "E157.MirrorP", {"position": v(2500, 28) * mm});
            skPoint(sketch, "E158.MirrorP", {"position": v(2500, 46) * mm});
            skPoint(sketch, "E159.MirrorP", {"position": v(2550, 72) * mm});
            skLineSegment(sketch, "E160.MirrorCS", {"start": v(2502, 72) * mm, "end": v(2502, 64) * mm});
            skLineSegment(sketch, "E161.MirrorCS", {"start": v(2550, 28) * mm, "end": v(2550, 36) * mm});
            skLineSegment(sketch, "E162.MirrorCS", {"start": v(2550, 82) * mm, "end": v(2550, 90) * mm});
            skPoint(sketch, "E163.MirrorP", {"position": v(2550, 64) * mm});
            skPoint(sketch, "E164.MirrorP", {"position": v(2500, 72) * mm});
            skPoint(sketch, "E165.MirrorP", {"position": v(2500, 18) * mm});
            skPoint(sketch, "E166.MirrorP", {"position": v(2550, 36) * mm});
            skLineSegment(sketch, "E167.MirrorCS", {"start": v(2548, 90) * mm, "end": v(2548, 82) * mm});
            skLineSegment(sketch, "E168.MirrorCS", {"start": v(2502, 18) * mm, "end": v(2502, 10) * mm});
            skLineSegment(sketch, "E169.MirrorCS", {"start": v(2502, 54) * mm, "end": v(2502, 46) * mm});
            skLineSegment(sketch, "E170.MirrorCS", {"start": v(2502, 36) * mm, "end": v(2502, 28) * mm});
            skPoint(sketch, "E171.MirrorP", {"position": v(2500, 54) * mm});
            skLineSegment(sketch, "E172.MirrorCS", {"start": v(2500, 82) * mm, "end": v(2500, 90) * mm});
            skPoint(sketch, "E173.MirrorP", {"position": v(2500, 10) * mm});
            skPoint(sketch, "E174.MirrorP", {"position": v(2550, 28) * mm});
            skPoint(sketch, "E175.MirrorP", {"position": v(2500, 64) * mm});
            skPoint(sketch, "E176.MirrorP", {"position": v(2550, 18) * mm});
            skLineSegment(sketch, "E177.MirrorCS", {"start": v(2548, 72) * mm, "end": v(2548, 64) * mm});
            skLineSegment(sketch, "E178.MirrorCS", {"start": v(2548, 18) * mm, "end": v(2548, 10) * mm});
            skLineSegment(sketch, "E179.MirrorCS", {"start": v(2500, 46) * mm, "end": v(2500, 54) * mm});
            skSolve(sketch);
        }
        {
            var Q0;
            Q0 = qSketchRegion(id + "F14", true);
            extrude(context, id + "F15", {"entities" : qUnion([Q0]), "operationType" : NewBodyOperationType.REMOVE, "endBound" : BoundingType.THROUGH_ALL, "oppositeDirection" : true, "depth" : 25 * mm, "offsetDistance" : 25 * mm});
        }
        {
            var Q0;
            Q0=makeQuery(id+"F1.opExtrude","CAP_EDGE",EDGE,{"disambiguationData":[OSD([sQuery(id+"F0.wireOp",EDGE,"E2.MirrorCS")])],"isStart":true});
            var Q1;
            Q1=makeQuery(id+"F1.opExtrude","CAP_EDGE",EDGE,{"disambiguationData":[OSD([sQuery(id+"F0.wireOp",EDGE,"E2.MirrorCS")])],"isStart":false});
            var Q2;
            {var subQ0=sQuery(id+"F0.wireOp",EDGE,"E3.MirrorCS");Q2=makeQuery(id+"F13.opFillet","BLEND_EDGE",EDGE,{"blendedFrom":[makeQuery(id+"F1.opExtrude","SWEPT_EDGE",EDGE,{"disambiguationData":[OSD([subQ0,sQuery(id+"F0.wireOp",EDGE,"E4.MirrorCS")])]}),makeQuery(id+"F1.opExtrude","CAP_EDGE",EDGE,{"disambiguationData":[OSD([subQ0])],"isStart":true})],"blendedInto":[]});}
            var Q3;
            {var subQ0=sQuery(id+"F0.wireOp",EDGE,"E3.MirrorCS");Q3=makeQuery(id+"F13.opFillet","BLEND_EDGE",EDGE,{"blendedFrom":[makeQuery(id+"F1.opExtrude","SWEPT_EDGE",EDGE,{"disambiguationData":[OSD([subQ0,sQuery(id+"F0.wireOp",EDGE,"E4.MirrorCS")])]}),makeQuery(id+"F1.opExtrude","CAP_EDGE",EDGE,{"disambiguationData":[OSD([subQ0])],"isStart":false})],"blendedInto":[]});}
            var Q4;
            {var subQ0=sQuery(id+"F2.wireOp",EDGE,"E7.top");var subQ1=makeQuery(id+"F3.opExtrude","SWEPT_FACE",FACE,{"disambiguationData":[OSD([subQ0])]});var subQ2=sQuery(id+"F2.wireOp",EDGE,"E7.left");Q4=makeQuery(id+"F13.opFillet","BLEND_EDGE",EDGE,{"blendedFrom":[makeQuery(id+"F7.boolean.opBoolean","SPLIT",EDGE,{"disambiguationData":[TD([subQ1])],"derivedFrom":makeQuery(id+"F3.opExtrude","CAP_EDGE",EDGE,{"disambiguationData":[OSD([subQ2])],"isStart":true})}),subQ1],"blendedInto":[subQ1]});}
            var Q5;
            Q5=makeQuery(id+"F3.opExtrude","CAP_EDGE",EDGE,{"disambiguationData":[OSD([sQuery(id+"F2.wireOp",EDGE,"E7.bottom")])],"isStart":true});
            fillet(context, id + "F16", {"entities" : qUnion([Q0, Q1, Q2, Q3, Q4, Q5]), "radius" : 2 * mm, "tangentPropagation" : true, "allowEdgeOverflow" : false});
        }
        {
            var Q0;
            Q0=makeQuery(id+"F1.opExtrude","SWEPT_BODY",BODY,{"disambiguationData":[OSD([sQuery(id+"F0.wireOp",EDGE,"E0.bottom"),sQuery(id+"F0.wireOp",EDGE,"E0.top"),sQuery(id+"F0.wireOp",EDGE,"E0.left"),sQuery(id+"F0.wireOp",EDGE,"E0.right")])]});
            var Q1;
            Q1=makeQuery(id+"F3.opExtrude","SWEPT_BODY",BODY,{"disambiguationData":[OSD([sQuery(id+"F2.wireOp",EDGE,"E6.bottom"),sQuery(id+"F2.wireOp",EDGE,"E6.top"),sQuery(id+"F2.wireOp",EDGE,"E6.left"),sQuery(id+"F2.wireOp",EDGE,"E6.right")])]});
            var Q2;
            Q2=makeQuery(id+"F3.opExtrude","SWEPT_BODY",BODY,{"disambiguationData":[OSD([sQuery(id+"F2.wireOp",EDGE,"E5.bottom"),sQuery(id+"F2.wireOp",EDGE,"E5.top"),sQuery(id+"F2.wireOp",EDGE,"E5.left"),sQuery(id+"F2.wireOp",EDGE,"E5.right")])]});
            var Q3;
            Q3=makeQuery(id+"F12.opExtrude","SWEPT_BODY",BODY,{"disambiguationData":[OSD([sQuery(id+"F11.wireOp",EDGE,"E67.0"),sQuery(id+"F11.wireOp",EDGE,"E67.1"),sQuery(id+"F11.wireOp",EDGE,"E67.2"),sQuery(id+"F11.wireOp",EDGE,"E67.3")])]});
            var Q4;
            Q4=makeQuery(id+"F12.opExtrude","SWEPT_BODY",BODY,{"disambiguationData":[OSD([sQuery(id+"F11.wireOp",EDGE,"E67.8"),sQuery(id+"F11.wireOp",EDGE,"E67.9"),sQuery(id+"F11.wireOp",EDGE,"E67.10"),sQuery(id+"F11.wireOp",EDGE,"E67.11")])]});
            deleteBodies(context, id + "F17", {"entities" : qUnion([Q0, Q1, Q2, Q3, Q4])});
        }
    });
